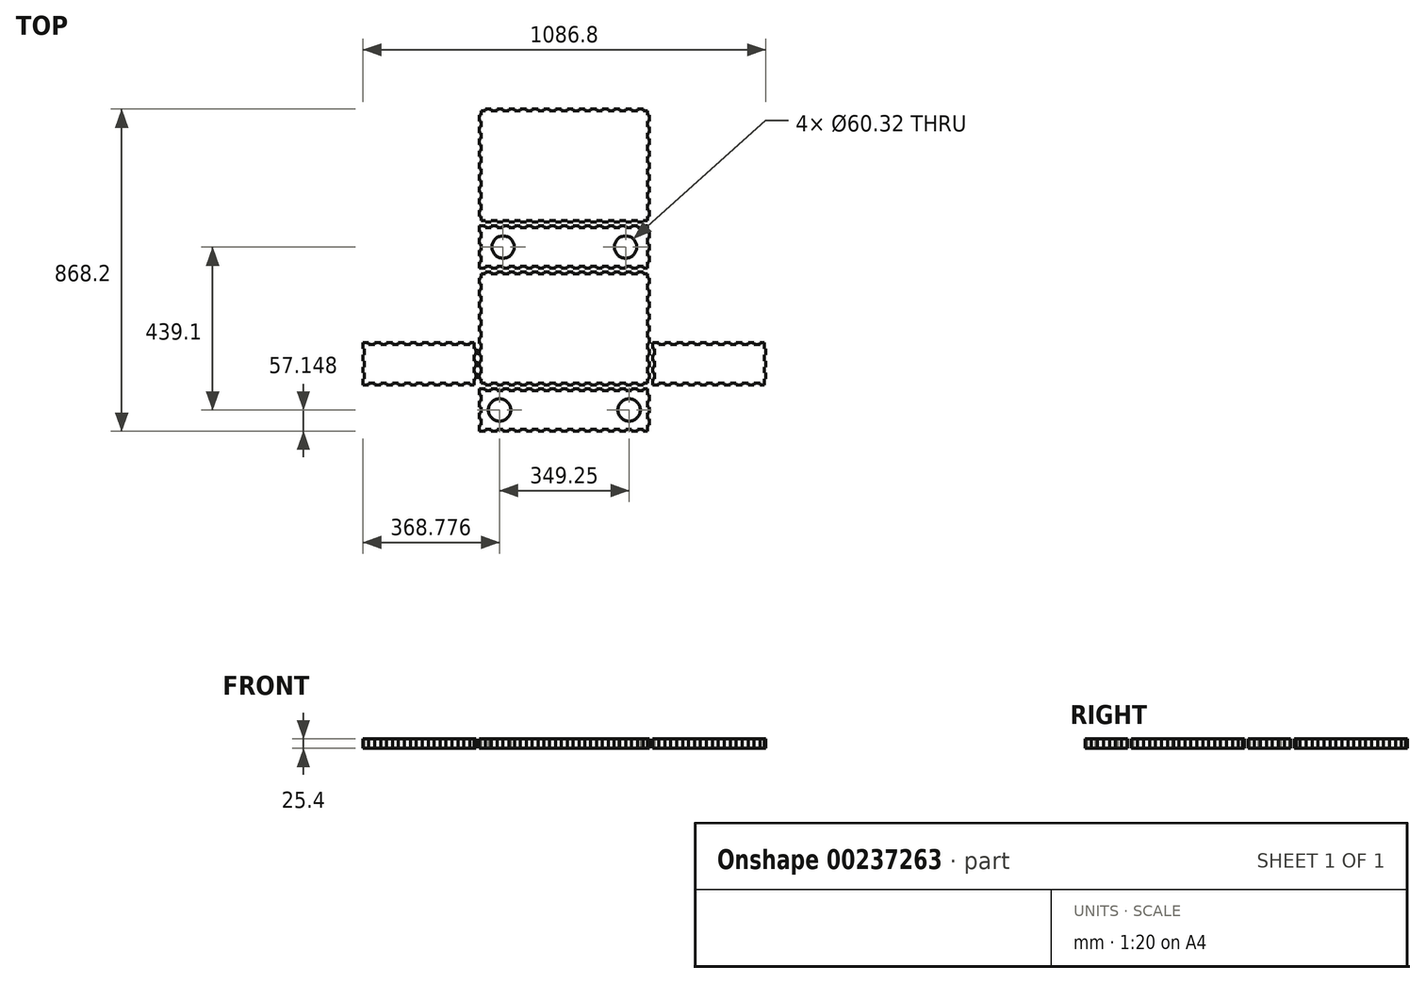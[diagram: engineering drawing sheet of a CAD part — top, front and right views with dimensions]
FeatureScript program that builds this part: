
annotation { "Feature Type Name" : "Feature", "Feature Type Description" : "" }
export const myFeature = defineFeature(function(context is Context, id is Id, definition is map)
    precondition{}
    {
        {
            var Q0;
            Q0=qCreatedBy(makeId("Top.planeOp"),FACE);
            var sketch = newSketch(context, id + "F0", { "sketchPlane" : qUnion([Q0])});
            skLineSegment(sketch, "E0", {"start": v(-228.6, -434.1) * mm, "end": v(-212.83, -434.1) * mm});
            skLineSegment(sketch, "E1", {"start": v(-212.83, -429.34) * mm, "end": v(-212.83, -434.1) * mm});
            skLineSegment(sketch, "E2", {"start": v(-212.83, -429.34) * mm, "end": v(-197.07, -429.34) * mm});
            skLineSegment(sketch, "E3", {"start": v(-197.07, -429.34) * mm, "end": v(-197.07, -434.1) * mm});
            skLineSegment(sketch, "E4", {"start": v(-197.07, -434.1) * mm, "end": v(-181.3, -434.1) * mm});
            skLineSegment(sketch, "E5", {"start": v(-181.3, -429.34) * mm, "end": v(-181.3, -434.1) * mm});
            skLineSegment(sketch, "E6", {"start": v(-181.3, -429.34) * mm, "end": v(-165.54, -429.34) * mm});
            skLineSegment(sketch, "E7", {"start": v(-165.54, -429.34) * mm, "end": v(-165.54, -434.1) * mm});
            skLineSegment(sketch, "E8", {"start": v(-165.54, -434.1) * mm, "end": v(-149.77, -434.1) * mm});
            skLineSegment(sketch, "E9", {"start": v(-149.77, -429.34) * mm, "end": v(-149.77, -434.1) * mm});
            skLineSegment(sketch, "E10", {"start": v(-149.77, -429.34) * mm, "end": v(-134, -429.34) * mm});
            skLineSegment(sketch, "E11", {"start": v(-134, -429.34) * mm, "end": v(-134, -434.1) * mm});
            skLineSegment(sketch, "E12", {"start": v(-134, -434.1) * mm, "end": v(-118.24, -434.1) * mm});
            skLineSegment(sketch, "E13", {"start": v(-118.24, -429.34) * mm, "end": v(-118.24, -434.1) * mm});
            skLineSegment(sketch, "E14", {"start": v(-118.24, -429.34) * mm, "end": v(-102.48, -429.34) * mm});
            skLineSegment(sketch, "E15", {"start": v(-102.48, -429.34) * mm, "end": v(-102.48, -434.1) * mm});
            skLineSegment(sketch, "E16", {"start": v(-102.48, -434.1) * mm, "end": v(-86.71, -434.1) * mm});
            skLineSegment(sketch, "E17", {"start": v(-86.71, -429.34) * mm, "end": v(-86.71, -434.1) * mm});
            skLineSegment(sketch, "E18", {"start": v(-86.71, -429.34) * mm, "end": v(-70.94, -429.34) * mm});
            skLineSegment(sketch, "E19", {"start": v(-70.94, -429.34) * mm, "end": v(-70.94, -434.1) * mm});
            skLineSegment(sketch, "E20", {"start": v(-70.94, -434.1) * mm, "end": v(-55.18, -434.1) * mm});
            skLineSegment(sketch, "E21", {"start": v(-55.18, -429.34) * mm, "end": v(-55.18, -434.1) * mm});
            skLineSegment(sketch, "E22", {"start": v(-55.18, -429.34) * mm, "end": v(-39.41, -429.34) * mm});
            skLineSegment(sketch, "E23", {"start": v(-39.41, -429.34) * mm, "end": v(-39.41, -434.1) * mm});
            skLineSegment(sketch, "E24", {"start": v(-39.41, -434.1) * mm, "end": v(-23.65, -434.1) * mm});
            skLineSegment(sketch, "E25", {"start": v(-23.65, -429.34) * mm, "end": v(-23.65, -434.1) * mm});
            skLineSegment(sketch, "E26", {"start": v(-23.65, -429.34) * mm, "end": v(-7.88, -429.34) * mm});
            skLineSegment(sketch, "E27", {"start": v(-7.88, -429.34) * mm, "end": v(-7.88, -434.1) * mm});
            skLineSegment(sketch, "E28", {"start": v(-7.88, -434.1) * mm, "end": v(7.88, -434.1) * mm});
            skLineSegment(sketch, "E29", {"start": v(7.88, -429.34) * mm, "end": v(7.88, -434.1) * mm});
            skLineSegment(sketch, "E30", {"start": v(7.88, -429.34) * mm, "end": v(23.65, -429.34) * mm});
            skLineSegment(sketch, "E31", {"start": v(23.65, -429.34) * mm, "end": v(23.65, -434.1) * mm});
            skLineSegment(sketch, "E32", {"start": v(23.65, -434.1) * mm, "end": v(39.42, -434.1) * mm});
            skLineSegment(sketch, "E33", {"start": v(39.42, -429.34) * mm, "end": v(39.42, -434.1) * mm});
            skLineSegment(sketch, "E34", {"start": v(39.42, -429.34) * mm, "end": v(55.18, -429.34) * mm});
            skLineSegment(sketch, "E35", {"start": v(55.18, -429.34) * mm, "end": v(55.18, -434.1) * mm});
            skLineSegment(sketch, "E36", {"start": v(55.18, -434.1) * mm, "end": v(70.95, -434.1) * mm});
            skLineSegment(sketch, "E37", {"start": v(70.95, -429.34) * mm, "end": v(70.95, -434.1) * mm});
            skLineSegment(sketch, "E38", {"start": v(70.95, -429.34) * mm, "end": v(86.7, -429.34) * mm});
            skLineSegment(sketch, "E39", {"start": v(86.7, -429.34) * mm, "end": v(86.7, -434.1) * mm});
            skLineSegment(sketch, "E40", {"start": v(86.7, -434.1) * mm, "end": v(102.48, -434.1) * mm});
            skLineSegment(sketch, "E41", {"start": v(102.48, -429.34) * mm, "end": v(102.48, -434.1) * mm});
            skLineSegment(sketch, "E42", {"start": v(102.48, -429.34) * mm, "end": v(118.24, -429.34) * mm});
            skLineSegment(sketch, "E43", {"start": v(118.24, -429.34) * mm, "end": v(118.24, -434.1) * mm});
            skLineSegment(sketch, "E44", {"start": v(118.24, -434.1) * mm, "end": v(134, -434.1) * mm});
            skLineSegment(sketch, "E45", {"start": v(134, -429.34) * mm, "end": v(134, -434.1) * mm});
            skLineSegment(sketch, "E46", {"start": v(134, -429.34) * mm, "end": v(149.77, -429.34) * mm});
            skLineSegment(sketch, "E47", {"start": v(149.77, -429.34) * mm, "end": v(149.77, -434.1) * mm});
            skLineSegment(sketch, "E48", {"start": v(149.77, -434.1) * mm, "end": v(165.54, -434.1) * mm});
            skLineSegment(sketch, "E49", {"start": v(165.54, -429.34) * mm, "end": v(165.54, -434.1) * mm});
            skLineSegment(sketch, "E50", {"start": v(165.54, -429.34) * mm, "end": v(181.3, -429.34) * mm});
            skLineSegment(sketch, "E51", {"start": v(181.3, -429.34) * mm, "end": v(181.3, -434.1) * mm});
            skLineSegment(sketch, "E52", {"start": v(181.3, -434.1) * mm, "end": v(197.07, -434.1) * mm});
            skLineSegment(sketch, "E53", {"start": v(197.07, -429.34) * mm, "end": v(197.07, -434.1) * mm});
            skLineSegment(sketch, "E54", {"start": v(197.07, -429.34) * mm, "end": v(212.83, -429.34) * mm});
            skLineSegment(sketch, "E55", {"start": v(212.83, -429.34) * mm, "end": v(212.83, -434.1) * mm});
            skLineSegment(sketch, "E56", {"start": v(212.83, -434.1) * mm, "end": v(223.84, -434.1) * mm});
            skLineSegment(sketch, "E57", {"start": v(-228.6, -319.8) * mm, "end": v(-212.83, -319.8) * mm});
            skLineSegment(sketch, "E58", {"start": v(-212.83, -319.8) * mm, "end": v(-212.83, -324.56) * mm});
            skLineSegment(sketch, "E59", {"start": v(-212.83, -324.56) * mm, "end": v(-197.07, -324.56) * mm});
            skLineSegment(sketch, "E60", {"start": v(-197.07, -319.8) * mm, "end": v(-197.07, -324.56) * mm});
            skLineSegment(sketch, "E61", {"start": v(-197.07, -319.8) * mm, "end": v(-181.3, -319.8) * mm});
            skLineSegment(sketch, "E62", {"start": v(-181.3, -319.8) * mm, "end": v(-181.3, -324.56) * mm});
            skLineSegment(sketch, "E63", {"start": v(-181.3, -324.56) * mm, "end": v(-165.54, -324.56) * mm});
            skLineSegment(sketch, "E64", {"start": v(-165.54, -319.8) * mm, "end": v(-165.54, -324.56) * mm});
            skLineSegment(sketch, "E65", {"start": v(-165.54, -319.8) * mm, "end": v(-149.77, -319.8) * mm});
            skLineSegment(sketch, "E66", {"start": v(-149.77, -319.8) * mm, "end": v(-149.77, -324.56) * mm});
            skLineSegment(sketch, "E67", {"start": v(-149.77, -324.56) * mm, "end": v(-134, -324.56) * mm});
            skLineSegment(sketch, "E68", {"start": v(-134, -319.8) * mm, "end": v(-134, -324.56) * mm});
            skLineSegment(sketch, "E69", {"start": v(-134, -319.8) * mm, "end": v(-118.24, -319.8) * mm});
            skLineSegment(sketch, "E70", {"start": v(-118.24, -319.8) * mm, "end": v(-118.24, -324.56) * mm});
            skLineSegment(sketch, "E71", {"start": v(-118.24, -324.56) * mm, "end": v(-102.48, -324.56) * mm});
            skLineSegment(sketch, "E72", {"start": v(-102.48, -319.8) * mm, "end": v(-102.48, -324.56) * mm});
            skLineSegment(sketch, "E73", {"start": v(-102.48, -319.8) * mm, "end": v(-86.71, -319.8) * mm});
            skLineSegment(sketch, "E74", {"start": v(-86.71, -319.8) * mm, "end": v(-86.71, -324.56) * mm});
            skLineSegment(sketch, "E75", {"start": v(-86.71, -324.56) * mm, "end": v(-70.94, -324.56) * mm});
            skLineSegment(sketch, "E76", {"start": v(-70.94, -319.8) * mm, "end": v(-70.94, -324.56) * mm});
            skLineSegment(sketch, "E77", {"start": v(-70.94, -319.8) * mm, "end": v(-55.18, -319.8) * mm});
            skLineSegment(sketch, "E78", {"start": v(-55.18, -319.8) * mm, "end": v(-55.18, -324.56) * mm});
            skLineSegment(sketch, "E79", {"start": v(-55.18, -324.56) * mm, "end": v(-39.41, -324.56) * mm});
            skLineSegment(sketch, "E80", {"start": v(-39.41, -319.8) * mm, "end": v(-39.41, -324.56) * mm});
            skLineSegment(sketch, "E81", {"start": v(-39.41, -319.8) * mm, "end": v(-23.65, -319.8) * mm});
            skLineSegment(sketch, "E82", {"start": v(-23.65, -319.8) * mm, "end": v(-23.65, -324.56) * mm});
            skLineSegment(sketch, "E83", {"start": v(-23.65, -324.56) * mm, "end": v(-7.88, -324.56) * mm});
            skLineSegment(sketch, "E84", {"start": v(-7.88, -319.8) * mm, "end": v(-7.88, -324.56) * mm});
            skLineSegment(sketch, "E85", {"start": v(-7.88, -319.8) * mm, "end": v(7.88, -319.8) * mm});
            skLineSegment(sketch, "E86", {"start": v(7.88, -319.8) * mm, "end": v(7.88, -324.56) * mm});
            skLineSegment(sketch, "E87", {"start": v(7.88, -324.56) * mm, "end": v(23.65, -324.56) * mm});
            skLineSegment(sketch, "E88", {"start": v(23.65, -319.8) * mm, "end": v(23.65, -324.56) * mm});
            skLineSegment(sketch, "E89", {"start": v(23.65, -319.8) * mm, "end": v(39.42, -319.8) * mm});
            skLineSegment(sketch, "E90", {"start": v(39.42, -319.8) * mm, "end": v(39.42, -324.56) * mm});
            skLineSegment(sketch, "E91", {"start": v(39.42, -324.56) * mm, "end": v(55.18, -324.56) * mm});
            skLineSegment(sketch, "E92", {"start": v(55.18, -319.8) * mm, "end": v(55.18, -324.56) * mm});
            skLineSegment(sketch, "E93", {"start": v(55.18, -319.8) * mm, "end": v(70.95, -319.8) * mm});
            skLineSegment(sketch, "E94", {"start": v(70.95, -319.8) * mm, "end": v(70.95, -324.56) * mm});
            skLineSegment(sketch, "E95", {"start": v(70.95, -324.56) * mm, "end": v(86.7, -324.56) * mm});
            skLineSegment(sketch, "E96", {"start": v(86.7, -319.8) * mm, "end": v(86.7, -324.56) * mm});
            skLineSegment(sketch, "E97", {"start": v(86.7, -319.8) * mm, "end": v(102.48, -319.8) * mm});
            skLineSegment(sketch, "E98", {"start": v(102.48, -319.8) * mm, "end": v(102.48, -324.56) * mm});
            skLineSegment(sketch, "E99", {"start": v(102.48, -324.56) * mm, "end": v(118.24, -324.56) * mm});
            skLineSegment(sketch, "E100", {"start": v(118.24, -319.8) * mm, "end": v(118.24, -324.56) * mm});
            skLineSegment(sketch, "E101", {"start": v(118.24, -319.8) * mm, "end": v(134, -319.8) * mm});
            skLineSegment(sketch, "E102", {"start": v(134, -319.8) * mm, "end": v(134, -324.56) * mm});
            skLineSegment(sketch, "E103", {"start": v(134, -324.56) * mm, "end": v(149.77, -324.56) * mm});
            skLineSegment(sketch, "E104", {"start": v(149.77, -319.8) * mm, "end": v(149.77, -324.56) * mm});
            skLineSegment(sketch, "E105", {"start": v(149.77, -319.8) * mm, "end": v(165.54, -319.8) * mm});
            skLineSegment(sketch, "E106", {"start": v(165.54, -319.8) * mm, "end": v(165.54, -324.56) * mm});
            skLineSegment(sketch, "E107", {"start": v(165.54, -324.56) * mm, "end": v(181.3, -324.56) * mm});
            skLineSegment(sketch, "E108", {"start": v(181.3, -319.8) * mm, "end": v(181.3, -324.56) * mm});
            skLineSegment(sketch, "E109", {"start": v(181.3, -319.8) * mm, "end": v(197.07, -319.8) * mm});
            skLineSegment(sketch, "E110", {"start": v(197.07, -319.8) * mm, "end": v(197.07, -324.56) * mm});
            skLineSegment(sketch, "E111", {"start": v(197.07, -324.56) * mm, "end": v(212.83, -324.56) * mm});
            skLineSegment(sketch, "E112", {"start": v(212.83, -319.8) * mm, "end": v(212.83, -324.56) * mm});
            skLineSegment(sketch, "E113", {"start": v(212.83, -319.8) * mm, "end": v(223.84, -319.8) * mm});
            skLineSegment(sketch, "E114", {"start": v(-228.6, -434.1) * mm, "end": v(-228.6, -417.77) * mm});
            skLineSegment(sketch, "E115", {"start": v(-223.84, -417.77) * mm, "end": v(-228.6, -417.77) * mm});
            skLineSegment(sketch, "E116", {"start": v(-223.84, -417.77) * mm, "end": v(-223.84, -401.44) * mm});
            skLineSegment(sketch, "E117", {"start": v(-223.84, -401.44) * mm, "end": v(-228.6, -401.44) * mm});
            skLineSegment(sketch, "E118", {"start": v(-228.6, -401.44) * mm, "end": v(-228.6, -385.12) * mm});
            skLineSegment(sketch, "E119", {"start": v(-223.84, -385.12) * mm, "end": v(-228.6, -385.12) * mm});
            skLineSegment(sketch, "E120", {"start": v(-223.84, -385.12) * mm, "end": v(-223.84, -368.79) * mm});
            skLineSegment(sketch, "E121", {"start": v(-223.84, -368.79) * mm, "end": v(-228.6, -368.79) * mm});
            skLineSegment(sketch, "E122", {"start": v(-228.6, -368.79) * mm, "end": v(-228.6, -352.46) * mm});
            skLineSegment(sketch, "E123", {"start": v(-223.84, -352.46) * mm, "end": v(-228.6, -352.46) * mm});
            skLineSegment(sketch, "E124", {"start": v(-223.84, -352.46) * mm, "end": v(-223.84, -336.13) * mm});
            skLineSegment(sketch, "E125", {"start": v(-223.84, -336.13) * mm, "end": v(-228.6, -336.13) * mm});
            skLineSegment(sketch, "E126", {"start": v(-228.6, -336.13) * mm, "end": v(-228.6, -319.8) * mm});
            skLineSegment(sketch, "E127", {"start": v(223.84, -434.1) * mm, "end": v(223.84, -417.77) * mm});
            skLineSegment(sketch, "E128", {"start": v(228.6, -417.77) * mm, "end": v(223.84, -417.77) * mm});
            skLineSegment(sketch, "E129", {"start": v(228.6, -417.77) * mm, "end": v(228.6, -401.44) * mm});
            skLineSegment(sketch, "E130", {"start": v(228.6, -401.44) * mm, "end": v(223.84, -401.44) * mm});
            skLineSegment(sketch, "E131", {"start": v(223.84, -401.44) * mm, "end": v(223.84, -385.12) * mm});
            skLineSegment(sketch, "E132", {"start": v(228.6, -385.12) * mm, "end": v(223.84, -385.12) * mm});
            skLineSegment(sketch, "E133", {"start": v(228.6, -385.12) * mm, "end": v(228.6, -368.79) * mm});
            skLineSegment(sketch, "E134", {"start": v(228.6, -368.79) * mm, "end": v(223.84, -368.79) * mm});
            skLineSegment(sketch, "E135", {"start": v(223.84, -368.79) * mm, "end": v(223.84, -352.46) * mm});
            skLineSegment(sketch, "E136", {"start": v(228.6, -352.46) * mm, "end": v(223.84, -352.46) * mm});
            skLineSegment(sketch, "E137", {"start": v(228.6, -352.46) * mm, "end": v(228.6, -336.13) * mm});
            skLineSegment(sketch, "E138", {"start": v(228.6, -336.13) * mm, "end": v(223.84, -336.13) * mm});
            skLineSegment(sketch, "E139", {"start": v(223.84, -336.13) * mm, "end": v(223.84, -319.8) * mm});
            skLineSegment(sketch, "E140", {"start": v(-543.4, -309.8) * mm, "end": v(-527.36, -309.8) * mm});
            skLineSegment(sketch, "E141", {"start": v(-527.36, -305.04) * mm, "end": v(-527.36, -309.8) * mm});
            skLineSegment(sketch, "E142", {"start": v(-527.36, -305.04) * mm, "end": v(-511.32, -305.04) * mm});
            skLineSegment(sketch, "E143", {"start": v(-511.32, -305.04) * mm, "end": v(-511.32, -309.8) * mm});
            skLineSegment(sketch, "E144", {"start": v(-511.32, -309.8) * mm, "end": v(-495.27, -309.8) * mm});
            skLineSegment(sketch, "E145", {"start": v(-495.27, -305.04) * mm, "end": v(-495.27, -309.8) * mm});
            skLineSegment(sketch, "E146", {"start": v(-495.27, -305.04) * mm, "end": v(-479.23, -305.04) * mm});
            skLineSegment(sketch, "E147", {"start": v(-479.23, -305.04) * mm, "end": v(-479.23, -309.8) * mm});
            skLineSegment(sketch, "E148", {"start": v(-479.23, -309.8) * mm, "end": v(-463.19, -309.8) * mm});
            skLineSegment(sketch, "E149", {"start": v(-463.19, -305.04) * mm, "end": v(-463.19, -309.8) * mm});
            skLineSegment(sketch, "E150", {"start": v(-463.19, -305.04) * mm, "end": v(-447.15, -305.04) * mm});
            skLineSegment(sketch, "E151", {"start": v(-447.15, -305.04) * mm, "end": v(-447.15, -309.8) * mm});
            skLineSegment(sketch, "E152", {"start": v(-447.15, -309.8) * mm, "end": v(-431.1, -309.8) * mm});
            skLineSegment(sketch, "E153", {"start": v(-431.1, -305.04) * mm, "end": v(-431.1, -309.8) * mm});
            skLineSegment(sketch, "E154", {"start": v(-431.1, -305.04) * mm, "end": v(-415.06, -305.04) * mm});
            skLineSegment(sketch, "E155", {"start": v(-415.06, -305.04) * mm, "end": v(-415.06, -309.8) * mm});
            skLineSegment(sketch, "E156", {"start": v(-415.06, -309.8) * mm, "end": v(-399.02, -309.8) * mm});
            skLineSegment(sketch, "E157", {"start": v(-399.02, -305.04) * mm, "end": v(-399.02, -309.8) * mm});
            skLineSegment(sketch, "E158", {"start": v(-399.02, -305.04) * mm, "end": v(-382.98, -305.04) * mm});
            skLineSegment(sketch, "E159", {"start": v(-382.98, -305.04) * mm, "end": v(-382.98, -309.8) * mm});
            skLineSegment(sketch, "E160", {"start": v(-382.98, -309.8) * mm, "end": v(-366.94, -309.8) * mm});
            skLineSegment(sketch, "E161", {"start": v(-366.94, -305.04) * mm, "end": v(-366.94, -309.8) * mm});
            skLineSegment(sketch, "E162", {"start": v(-366.94, -305.04) * mm, "end": v(-350.9, -305.04) * mm});
            skLineSegment(sketch, "E163", {"start": v(-350.9, -305.04) * mm, "end": v(-350.9, -309.8) * mm});
            skLineSegment(sketch, "E164", {"start": v(-350.9, -309.8) * mm, "end": v(-334.85, -309.8) * mm});
            skLineSegment(sketch, "E165", {"start": v(-334.85, -305.04) * mm, "end": v(-334.85, -309.8) * mm});
            skLineSegment(sketch, "E166", {"start": v(-334.85, -305.04) * mm, "end": v(-318.81, -305.04) * mm});
            skLineSegment(sketch, "E167", {"start": v(-318.81, -305.04) * mm, "end": v(-318.81, -309.8) * mm});
            skLineSegment(sketch, "E168", {"start": v(-318.81, -309.8) * mm, "end": v(-302.77, -309.8) * mm});
            skLineSegment(sketch, "E169", {"start": v(-302.77, -305.04) * mm, "end": v(-302.77, -309.8) * mm});
            skLineSegment(sketch, "E170", {"start": v(-302.77, -305.04) * mm, "end": v(-286.73, -305.04) * mm});
            skLineSegment(sketch, "E171", {"start": v(-286.73, -305.04) * mm, "end": v(-286.73, -309.8) * mm});
            skLineSegment(sketch, "E172", {"start": v(-286.73, -309.8) * mm, "end": v(-270.69, -309.8) * mm});
            skLineSegment(sketch, "E173", {"start": v(-270.69, -305.04) * mm, "end": v(-270.69, -309.8) * mm});
            skLineSegment(sketch, "E174", {"start": v(-270.69, -305.04) * mm, "end": v(-254.64, -305.04) * mm});
            skLineSegment(sketch, "E175", {"start": v(-254.64, -305.04) * mm, "end": v(-254.64, -309.8) * mm});
            skLineSegment(sketch, "E176", {"start": v(-254.64, -309.8) * mm, "end": v(-243.36, -309.8) * mm});
            skLineSegment(sketch, "E177", {"start": v(-543.4, -195.5) * mm, "end": v(-527.36, -195.5) * mm});
            skLineSegment(sketch, "E178", {"start": v(-527.36, -195.5) * mm, "end": v(-527.36, -200.26) * mm});
            skLineSegment(sketch, "E179", {"start": v(-527.36, -200.26) * mm, "end": v(-511.32, -200.26) * mm});
            skLineSegment(sketch, "E180", {"start": v(-511.32, -195.5) * mm, "end": v(-511.32, -200.26) * mm});
            skLineSegment(sketch, "E181", {"start": v(-511.32, -195.5) * mm, "end": v(-495.27, -195.5) * mm});
            skLineSegment(sketch, "E182", {"start": v(-495.27, -195.5) * mm, "end": v(-495.27, -200.26) * mm});
            skLineSegment(sketch, "E183", {"start": v(-495.27, -200.26) * mm, "end": v(-479.23, -200.26) * mm});
            skLineSegment(sketch, "E184", {"start": v(-479.23, -195.5) * mm, "end": v(-479.23, -200.26) * mm});
            skLineSegment(sketch, "E185", {"start": v(-479.23, -195.5) * mm, "end": v(-463.19, -195.5) * mm});
            skLineSegment(sketch, "E186", {"start": v(-463.19, -195.5) * mm, "end": v(-463.19, -200.26) * mm});
            skLineSegment(sketch, "E187", {"start": v(-463.19, -200.26) * mm, "end": v(-447.15, -200.26) * mm});
            skLineSegment(sketch, "E188", {"start": v(-447.15, -195.5) * mm, "end": v(-447.15, -200.26) * mm});
            skLineSegment(sketch, "E189", {"start": v(-447.15, -195.5) * mm, "end": v(-431.1, -195.5) * mm});
            skLineSegment(sketch, "E190", {"start": v(-431.1, -195.5) * mm, "end": v(-431.1, -200.26) * mm});
            skLineSegment(sketch, "E191", {"start": v(-431.1, -200.26) * mm, "end": v(-415.06, -200.26) * mm});
            skLineSegment(sketch, "E192", {"start": v(-415.06, -195.5) * mm, "end": v(-415.06, -200.26) * mm});
            skLineSegment(sketch, "E193", {"start": v(-415.06, -195.5) * mm, "end": v(-399.02, -195.5) * mm});
            skLineSegment(sketch, "E194", {"start": v(-399.02, -195.5) * mm, "end": v(-399.02, -200.26) * mm});
            skLineSegment(sketch, "E195", {"start": v(-399.02, -200.26) * mm, "end": v(-382.98, -200.26) * mm});
            skLineSegment(sketch, "E196", {"start": v(-382.98, -195.5) * mm, "end": v(-382.98, -200.26) * mm});
            skLineSegment(sketch, "E197", {"start": v(-382.98, -195.5) * mm, "end": v(-366.94, -195.5) * mm});
            skLineSegment(sketch, "E198", {"start": v(-366.94, -195.5) * mm, "end": v(-366.94, -200.26) * mm});
            skLineSegment(sketch, "E199", {"start": v(-366.94, -200.26) * mm, "end": v(-350.9, -200.26) * mm});
            skLineSegment(sketch, "E200", {"start": v(-350.9, -195.5) * mm, "end": v(-350.9, -200.26) * mm});
            skLineSegment(sketch, "E201", {"start": v(-350.9, -195.5) * mm, "end": v(-334.85, -195.5) * mm});
            skLineSegment(sketch, "E202", {"start": v(-334.85, -195.5) * mm, "end": v(-334.85, -200.26) * mm});
            skLineSegment(sketch, "E203", {"start": v(-334.85, -200.26) * mm, "end": v(-318.81, -200.26) * mm});
            skLineSegment(sketch, "E204", {"start": v(-318.81, -195.5) * mm, "end": v(-318.81, -200.26) * mm});
            skLineSegment(sketch, "E205", {"start": v(-318.81, -195.5) * mm, "end": v(-302.77, -195.5) * mm});
            skLineSegment(sketch, "E206", {"start": v(-302.77, -195.5) * mm, "end": v(-302.77, -200.26) * mm});
            skLineSegment(sketch, "E207", {"start": v(-302.77, -200.26) * mm, "end": v(-286.73, -200.26) * mm});
            skLineSegment(sketch, "E208", {"start": v(-286.73, -195.5) * mm, "end": v(-286.73, -200.26) * mm});
            skLineSegment(sketch, "E209", {"start": v(-286.73, -195.5) * mm, "end": v(-270.69, -195.5) * mm});
            skLineSegment(sketch, "E210", {"start": v(-270.69, -195.5) * mm, "end": v(-270.69, -200.26) * mm});
            skLineSegment(sketch, "E211", {"start": v(-270.69, -200.26) * mm, "end": v(-254.64, -200.26) * mm});
            skLineSegment(sketch, "E212", {"start": v(-254.64, -195.5) * mm, "end": v(-254.64, -200.26) * mm});
            skLineSegment(sketch, "E213", {"start": v(-254.64, -195.5) * mm, "end": v(-243.36, -195.5) * mm});
            skLineSegment(sketch, "E214", {"start": v(-543.4, -309.8) * mm, "end": v(-543.4, -293.47) * mm});
            skLineSegment(sketch, "E215", {"start": v(-538.64, -293.47) * mm, "end": v(-543.4, -293.47) * mm});
            skLineSegment(sketch, "E216", {"start": v(-538.64, -293.47) * mm, "end": v(-538.64, -277.14) * mm});
            skLineSegment(sketch, "E217", {"start": v(-538.64, -277.14) * mm, "end": v(-543.4, -277.14) * mm});
            skLineSegment(sketch, "E218", {"start": v(-543.4, -277.14) * mm, "end": v(-543.4, -260.82) * mm});
            skLineSegment(sketch, "E219", {"start": v(-538.64, -260.82) * mm, "end": v(-543.4, -260.82) * mm});
            skLineSegment(sketch, "E220", {"start": v(-538.64, -260.82) * mm, "end": v(-538.64, -244.49) * mm});
            skLineSegment(sketch, "E221", {"start": v(-538.64, -244.49) * mm, "end": v(-543.4, -244.49) * mm});
            skLineSegment(sketch, "E222", {"start": v(-543.4, -244.49) * mm, "end": v(-543.4, -228.16) * mm});
            skLineSegment(sketch, "E223", {"start": v(-538.64, -228.16) * mm, "end": v(-543.4, -228.16) * mm});
            skLineSegment(sketch, "E224", {"start": v(-538.64, -228.16) * mm, "end": v(-538.64, -211.83) * mm});
            skLineSegment(sketch, "E225", {"start": v(-538.64, -211.83) * mm, "end": v(-543.4, -211.83) * mm});
            skLineSegment(sketch, "E226", {"start": v(-543.4, -211.83) * mm, "end": v(-543.4, -195.5) * mm});
            skLineSegment(sketch, "E227", {"start": v(-243.36, -309.8) * mm, "end": v(-243.36, -293.47) * mm});
            skLineSegment(sketch, "E228", {"start": v(-238.6, -293.47) * mm, "end": v(-243.36, -293.47) * mm});
            skLineSegment(sketch, "E229", {"start": v(-238.6, -293.47) * mm, "end": v(-238.6, -277.14) * mm});
            skLineSegment(sketch, "E230", {"start": v(-238.6, -277.14) * mm, "end": v(-243.36, -277.14) * mm});
            skLineSegment(sketch, "E231", {"start": v(-243.36, -277.14) * mm, "end": v(-243.36, -260.82) * mm});
            skLineSegment(sketch, "E232", {"start": v(-238.6, -260.82) * mm, "end": v(-243.36, -260.82) * mm});
            skLineSegment(sketch, "E233", {"start": v(-238.6, -260.82) * mm, "end": v(-238.6, -244.49) * mm});
            skLineSegment(sketch, "E234", {"start": v(-238.6, -244.49) * mm, "end": v(-243.36, -244.49) * mm});
            skLineSegment(sketch, "E235", {"start": v(-243.36, -244.49) * mm, "end": v(-243.36, -228.16) * mm});
            skLineSegment(sketch, "E236", {"start": v(-238.6, -228.16) * mm, "end": v(-243.36, -228.16) * mm});
            skLineSegment(sketch, "E237", {"start": v(-238.6, -228.16) * mm, "end": v(-238.6, -211.83) * mm});
            skLineSegment(sketch, "E238", {"start": v(-238.6, -211.83) * mm, "end": v(-243.36, -211.83) * mm});
            skLineSegment(sketch, "E239", {"start": v(-243.36, -211.83) * mm, "end": v(-243.36, -195.5) * mm});
            skLineSegment(sketch, "E240", {"start": v(-223.84, -305.04) * mm, "end": v(-212.83, -305.04) * mm});
            skLineSegment(sketch, "E241", {"start": v(-212.83, -305.04) * mm, "end": v(-212.83, -309.8) * mm});
            skLineSegment(sketch, "E242", {"start": v(-212.83, -309.8) * mm, "end": v(-197.07, -309.8) * mm});
            skLineSegment(sketch, "E243", {"start": v(-197.07, -305.04) * mm, "end": v(-197.07, -309.8) * mm});
            skLineSegment(sketch, "E244", {"start": v(-197.07, -305.04) * mm, "end": v(-181.3, -305.04) * mm});
            skLineSegment(sketch, "E245", {"start": v(-181.3, -305.04) * mm, "end": v(-181.3, -309.8) * mm});
            skLineSegment(sketch, "E246", {"start": v(-181.3, -309.8) * mm, "end": v(-165.54, -309.8) * mm});
            skLineSegment(sketch, "E247", {"start": v(-165.54, -305.04) * mm, "end": v(-165.54, -309.8) * mm});
            skLineSegment(sketch, "E248", {"start": v(-165.54, -305.04) * mm, "end": v(-149.77, -305.04) * mm});
            skLineSegment(sketch, "E249", {"start": v(-149.77, -305.04) * mm, "end": v(-149.77, -309.8) * mm});
            skLineSegment(sketch, "E250", {"start": v(-149.77, -309.8) * mm, "end": v(-134, -309.8) * mm});
            skLineSegment(sketch, "E251", {"start": v(-134, -305.04) * mm, "end": v(-134, -309.8) * mm});
            skLineSegment(sketch, "E252", {"start": v(-134, -305.04) * mm, "end": v(-118.24, -305.04) * mm});
            skLineSegment(sketch, "E253", {"start": v(-118.24, -305.04) * mm, "end": v(-118.24, -309.8) * mm});
            skLineSegment(sketch, "E254", {"start": v(-118.24, -309.8) * mm, "end": v(-102.48, -309.8) * mm});
            skLineSegment(sketch, "E255", {"start": v(-102.48, -305.04) * mm, "end": v(-102.48, -309.8) * mm});
            skLineSegment(sketch, "E256", {"start": v(-102.48, -305.04) * mm, "end": v(-86.71, -305.04) * mm});
            skLineSegment(sketch, "E257", {"start": v(-86.71, -305.04) * mm, "end": v(-86.71, -309.8) * mm});
            skLineSegment(sketch, "E258", {"start": v(-86.71, -309.8) * mm, "end": v(-70.94, -309.8) * mm});
            skLineSegment(sketch, "E259", {"start": v(-70.94, -305.04) * mm, "end": v(-70.94, -309.8) * mm});
            skLineSegment(sketch, "E260", {"start": v(-70.94, -305.04) * mm, "end": v(-55.18, -305.04) * mm});
            skLineSegment(sketch, "E261", {"start": v(-55.18, -305.04) * mm, "end": v(-55.18, -309.8) * mm});
            skLineSegment(sketch, "E262", {"start": v(-55.18, -309.8) * mm, "end": v(-39.41, -309.8) * mm});
            skLineSegment(sketch, "E263", {"start": v(-39.41, -305.04) * mm, "end": v(-39.41, -309.8) * mm});
            skLineSegment(sketch, "E264", {"start": v(-39.41, -305.04) * mm, "end": v(-23.65, -305.04) * mm});
            skLineSegment(sketch, "E265", {"start": v(-23.65, -305.04) * mm, "end": v(-23.65, -309.8) * mm});
            skLineSegment(sketch, "E266", {"start": v(-23.65, -309.8) * mm, "end": v(-7.88, -309.8) * mm});
            skLineSegment(sketch, "E267", {"start": v(-7.88, -305.04) * mm, "end": v(-7.88, -309.8) * mm});
            skLineSegment(sketch, "E268", {"start": v(-7.88, -305.04) * mm, "end": v(7.88, -305.04) * mm});
            skLineSegment(sketch, "E269", {"start": v(7.88, -305.04) * mm, "end": v(7.88, -309.8) * mm});
            skLineSegment(sketch, "E270", {"start": v(7.88, -309.8) * mm, "end": v(23.65, -309.8) * mm});
            skLineSegment(sketch, "E271", {"start": v(23.65, -305.04) * mm, "end": v(23.65, -309.8) * mm});
            skLineSegment(sketch, "E272", {"start": v(23.65, -305.04) * mm, "end": v(39.42, -305.04) * mm});
            skLineSegment(sketch, "E273", {"start": v(39.42, -305.04) * mm, "end": v(39.42, -309.8) * mm});
            skLineSegment(sketch, "E274", {"start": v(39.42, -309.8) * mm, "end": v(55.18, -309.8) * mm});
            skLineSegment(sketch, "E275", {"start": v(55.18, -305.04) * mm, "end": v(55.18, -309.8) * mm});
            skLineSegment(sketch, "E276", {"start": v(55.18, -305.04) * mm, "end": v(70.95, -305.04) * mm});
            skLineSegment(sketch, "E277", {"start": v(70.95, -305.04) * mm, "end": v(70.95, -309.8) * mm});
            skLineSegment(sketch, "E278", {"start": v(70.95, -309.8) * mm, "end": v(86.7, -309.8) * mm});
            skLineSegment(sketch, "E279", {"start": v(86.7, -305.04) * mm, "end": v(86.7, -309.8) * mm});
            skLineSegment(sketch, "E280", {"start": v(86.7, -305.04) * mm, "end": v(102.48, -305.04) * mm});
            skLineSegment(sketch, "E281", {"start": v(102.48, -305.04) * mm, "end": v(102.48, -309.8) * mm});
            skLineSegment(sketch, "E282", {"start": v(102.48, -309.8) * mm, "end": v(118.24, -309.8) * mm});
            skLineSegment(sketch, "E283", {"start": v(118.24, -305.04) * mm, "end": v(118.24, -309.8) * mm});
            skLineSegment(sketch, "E284", {"start": v(118.24, -305.04) * mm, "end": v(134, -305.04) * mm});
            skLineSegment(sketch, "E285", {"start": v(134, -305.04) * mm, "end": v(134, -309.8) * mm});
            skLineSegment(sketch, "E286", {"start": v(134, -309.8) * mm, "end": v(149.77, -309.8) * mm});
            skLineSegment(sketch, "E287", {"start": v(149.77, -305.04) * mm, "end": v(149.77, -309.8) * mm});
            skLineSegment(sketch, "E288", {"start": v(149.77, -305.04) * mm, "end": v(165.54, -305.04) * mm});
            skLineSegment(sketch, "E289", {"start": v(165.54, -305.04) * mm, "end": v(165.54, -309.8) * mm});
            skLineSegment(sketch, "E290", {"start": v(165.54, -309.8) * mm, "end": v(181.3, -309.8) * mm});
            skLineSegment(sketch, "E291", {"start": v(181.3, -305.04) * mm, "end": v(181.3, -309.8) * mm});
            skLineSegment(sketch, "E292", {"start": v(181.3, -305.04) * mm, "end": v(197.07, -305.04) * mm});
            skLineSegment(sketch, "E293", {"start": v(197.07, -305.04) * mm, "end": v(197.07, -309.8) * mm});
            skLineSegment(sketch, "E294", {"start": v(197.07, -309.8) * mm, "end": v(212.83, -309.8) * mm});
            skLineSegment(sketch, "E295", {"start": v(212.83, -305.04) * mm, "end": v(212.83, -309.8) * mm});
            skLineSegment(sketch, "E296", {"start": v(212.83, -305.04) * mm, "end": v(223.84, -305.04) * mm});
            skLineSegment(sketch, "E297", {"start": v(-223.84, -9.76) * mm, "end": v(-212.83, -9.76) * mm});
            skLineSegment(sketch, "E298", {"start": v(-212.83, -5) * mm, "end": v(-212.83, -9.76) * mm});
            skLineSegment(sketch, "E299", {"start": v(-212.83, -5) * mm, "end": v(-197.07, -5) * mm});
            skLineSegment(sketch, "E300", {"start": v(-197.07, -5) * mm, "end": v(-197.07, -9.76) * mm});
            skLineSegment(sketch, "E301", {"start": v(-197.07, -9.76) * mm, "end": v(-181.3, -9.76) * mm});
            skLineSegment(sketch, "E302", {"start": v(-181.3, -5) * mm, "end": v(-181.3, -9.76) * mm});
            skLineSegment(sketch, "E303", {"start": v(-181.3, -5) * mm, "end": v(-165.54, -5) * mm});
            skLineSegment(sketch, "E304", {"start": v(-165.54, -5) * mm, "end": v(-165.54, -9.76) * mm});
            skLineSegment(sketch, "E305", {"start": v(-165.54, -9.76) * mm, "end": v(-149.77, -9.76) * mm});
            skLineSegment(sketch, "E306", {"start": v(-149.77, -5) * mm, "end": v(-149.77, -9.76) * mm});
            skLineSegment(sketch, "E307", {"start": v(-149.77, -5) * mm, "end": v(-134, -5) * mm});
            skLineSegment(sketch, "E308", {"start": v(-134, -5) * mm, "end": v(-134, -9.76) * mm});
            skLineSegment(sketch, "E309", {"start": v(-134, -9.76) * mm, "end": v(-118.24, -9.76) * mm});
            skLineSegment(sketch, "E310", {"start": v(-118.24, -5) * mm, "end": v(-118.24, -9.76) * mm});
            skLineSegment(sketch, "E311", {"start": v(-118.24, -5) * mm, "end": v(-102.48, -5) * mm});
            skLineSegment(sketch, "E312", {"start": v(-102.48, -5) * mm, "end": v(-102.48, -9.76) * mm});
            skLineSegment(sketch, "E313", {"start": v(-102.48, -9.76) * mm, "end": v(-86.71, -9.76) * mm});
            skLineSegment(sketch, "E314", {"start": v(-86.71, -5) * mm, "end": v(-86.71, -9.76) * mm});
            skLineSegment(sketch, "E315", {"start": v(-86.71, -5) * mm, "end": v(-70.94, -5) * mm});
            skLineSegment(sketch, "E316", {"start": v(-70.94, -5) * mm, "end": v(-70.94, -9.76) * mm});
            skLineSegment(sketch, "E317", {"start": v(-70.94, -9.76) * mm, "end": v(-55.18, -9.76) * mm});
            skLineSegment(sketch, "E318", {"start": v(-55.18, -5) * mm, "end": v(-55.18, -9.76) * mm});
            skLineSegment(sketch, "E319", {"start": v(-55.18, -5) * mm, "end": v(-39.41, -5) * mm});
            skLineSegment(sketch, "E320", {"start": v(-39.41, -5) * mm, "end": v(-39.41, -9.76) * mm});
            skLineSegment(sketch, "E321", {"start": v(-39.41, -9.76) * mm, "end": v(-23.65, -9.76) * mm});
            skLineSegment(sketch, "E322", {"start": v(-23.65, -5) * mm, "end": v(-23.65, -9.76) * mm});
            skLineSegment(sketch, "E323", {"start": v(-23.65, -5) * mm, "end": v(-7.88, -5) * mm});
            skLineSegment(sketch, "E324", {"start": v(-7.88, -5) * mm, "end": v(-7.88, -9.76) * mm});
            skLineSegment(sketch, "E325", {"start": v(-7.88, -9.76) * mm, "end": v(7.88, -9.76) * mm});
            skLineSegment(sketch, "E326", {"start": v(7.88, -5) * mm, "end": v(7.88, -9.76) * mm});
            skLineSegment(sketch, "E327", {"start": v(7.88, -5) * mm, "end": v(23.65, -5) * mm});
            skLineSegment(sketch, "E328", {"start": v(23.65, -5) * mm, "end": v(23.65, -9.76) * mm});
            skLineSegment(sketch, "E329", {"start": v(23.65, -9.76) * mm, "end": v(39.42, -9.76) * mm});
            skLineSegment(sketch, "E330", {"start": v(39.42, -5) * mm, "end": v(39.42, -9.76) * mm});
            skLineSegment(sketch, "E331", {"start": v(39.42, -5) * mm, "end": v(55.18, -5) * mm});
            skLineSegment(sketch, "E332", {"start": v(55.18, -5) * mm, "end": v(55.18, -9.76) * mm});
            skLineSegment(sketch, "E333", {"start": v(55.18, -9.76) * mm, "end": v(70.95, -9.76) * mm});
            skLineSegment(sketch, "E334", {"start": v(70.95, -5) * mm, "end": v(70.95, -9.76) * mm});
            skLineSegment(sketch, "E335", {"start": v(70.95, -5) * mm, "end": v(86.7, -5) * mm});
            skLineSegment(sketch, "E336", {"start": v(86.7, -5) * mm, "end": v(86.7, -9.76) * mm});
            skLineSegment(sketch, "E337", {"start": v(86.7, -9.76) * mm, "end": v(102.48, -9.76) * mm});
            skLineSegment(sketch, "E338", {"start": v(102.48, -5) * mm, "end": v(102.48, -9.76) * mm});
            skLineSegment(sketch, "E339", {"start": v(102.48, -5) * mm, "end": v(118.24, -5) * mm});
            skLineSegment(sketch, "E340", {"start": v(118.24, -5) * mm, "end": v(118.24, -9.76) * mm});
            skLineSegment(sketch, "E341", {"start": v(118.24, -9.76) * mm, "end": v(134, -9.76) * mm});
            skLineSegment(sketch, "E342", {"start": v(134, -5) * mm, "end": v(134, -9.76) * mm});
            skLineSegment(sketch, "E343", {"start": v(134, -5) * mm, "end": v(149.77, -5) * mm});
            skLineSegment(sketch, "E344", {"start": v(149.77, -5) * mm, "end": v(149.77, -9.76) * mm});
            skLineSegment(sketch, "E345", {"start": v(149.77, -9.76) * mm, "end": v(165.54, -9.76) * mm});
            skLineSegment(sketch, "E346", {"start": v(165.54, -5) * mm, "end": v(165.54, -9.76) * mm});
            skLineSegment(sketch, "E347", {"start": v(165.54, -5) * mm, "end": v(181.3, -5) * mm});
            skLineSegment(sketch, "E348", {"start": v(181.3, -5) * mm, "end": v(181.3, -9.76) * mm});
            skLineSegment(sketch, "E349", {"start": v(181.3, -9.76) * mm, "end": v(197.07, -9.76) * mm});
            skLineSegment(sketch, "E350", {"start": v(197.07, -5) * mm, "end": v(197.07, -9.76) * mm});
            skLineSegment(sketch, "E351", {"start": v(197.07, -5) * mm, "end": v(212.83, -5) * mm});
            skLineSegment(sketch, "E352", {"start": v(212.83, -5) * mm, "end": v(212.83, -9.76) * mm});
            skLineSegment(sketch, "E353", {"start": v(212.83, -9.76) * mm, "end": v(223.84, -9.76) * mm});
            skLineSegment(sketch, "E354", {"start": v(-223.84, -305.04) * mm, "end": v(-223.84, -293.76) * mm});
            skLineSegment(sketch, "E355", {"start": v(-223.84, -293.76) * mm, "end": v(-228.6, -293.76) * mm});
            skLineSegment(sketch, "E356", {"start": v(-228.6, -293.76) * mm, "end": v(-228.6, -277.72) * mm});
            skLineSegment(sketch, "E357", {"start": v(-223.84, -277.72) * mm, "end": v(-228.6, -277.72) * mm});
            skLineSegment(sketch, "E358", {"start": v(-223.84, -277.72) * mm, "end": v(-223.84, -261.68) * mm});
            skLineSegment(sketch, "E359", {"start": v(-223.84, -261.68) * mm, "end": v(-228.6, -261.68) * mm});
            skLineSegment(sketch, "E360", {"start": v(-228.6, -261.68) * mm, "end": v(-228.6, -245.63) * mm});
            skLineSegment(sketch, "E361", {"start": v(-223.84, -245.63) * mm, "end": v(-228.6, -245.63) * mm});
            skLineSegment(sketch, "E362", {"start": v(-223.84, -245.63) * mm, "end": v(-223.84, -229.6) * mm});
            skLineSegment(sketch, "E363", {"start": v(-223.84, -229.6) * mm, "end": v(-228.6, -229.6) * mm});
            skLineSegment(sketch, "E364", {"start": v(-228.6, -229.6) * mm, "end": v(-228.6, -213.55) * mm});
            skLineSegment(sketch, "E365", {"start": v(-223.84, -213.55) * mm, "end": v(-228.6, -213.55) * mm});
            skLineSegment(sketch, "E366", {"start": v(-223.84, -213.55) * mm, "end": v(-223.84, -197.5) * mm});
            skLineSegment(sketch, "E367", {"start": v(-223.84, -197.5) * mm, "end": v(-228.6, -197.5) * mm});
            skLineSegment(sketch, "E368", {"start": v(-228.6, -197.5) * mm, "end": v(-228.6, -181.47) * mm});
            skLineSegment(sketch, "E369", {"start": v(-223.84, -181.47) * mm, "end": v(-228.6, -181.47) * mm});
            skLineSegment(sketch, "E370", {"start": v(-223.84, -181.47) * mm, "end": v(-223.84, -165.42) * mm});
            skLineSegment(sketch, "E371", {"start": v(-223.84, -165.42) * mm, "end": v(-228.6, -165.42) * mm});
            skLineSegment(sketch, "E372", {"start": v(-228.6, -165.42) * mm, "end": v(-228.6, -149.38) * mm});
            skLineSegment(sketch, "E373", {"start": v(-223.84, -149.38) * mm, "end": v(-228.6, -149.38) * mm});
            skLineSegment(sketch, "E374", {"start": v(-223.84, -149.38) * mm, "end": v(-223.84, -133.34) * mm});
            skLineSegment(sketch, "E375", {"start": v(-223.84, -133.34) * mm, "end": v(-228.6, -133.34) * mm});
            skLineSegment(sketch, "E376", {"start": v(-228.6, -133.34) * mm, "end": v(-228.6, -117.3) * mm});
            skLineSegment(sketch, "E377", {"start": v(-223.84, -117.3) * mm, "end": v(-228.6, -117.3) * mm});
            skLineSegment(sketch, "E378", {"start": v(-223.84, -117.3) * mm, "end": v(-223.84, -101.25) * mm});
            skLineSegment(sketch, "E379", {"start": v(-223.84, -101.25) * mm, "end": v(-228.6, -101.25) * mm});
            skLineSegment(sketch, "E380", {"start": v(-228.6, -101.25) * mm, "end": v(-228.6, -85.21) * mm});
            skLineSegment(sketch, "E381", {"start": v(-223.84, -85.21) * mm, "end": v(-228.6, -85.21) * mm});
            skLineSegment(sketch, "E382", {"start": v(-223.84, -85.21) * mm, "end": v(-223.84, -69.17) * mm});
            skLineSegment(sketch, "E383", {"start": v(-223.84, -69.17) * mm, "end": v(-228.6, -69.17) * mm});
            skLineSegment(sketch, "E384", {"start": v(-228.6, -69.17) * mm, "end": v(-228.6, -53.13) * mm});
            skLineSegment(sketch, "E385", {"start": v(-223.84, -53.13) * mm, "end": v(-228.6, -53.13) * mm});
            skLineSegment(sketch, "E386", {"start": v(-223.84, -53.13) * mm, "end": v(-223.84, -37.08) * mm});
            skLineSegment(sketch, "E387", {"start": v(-223.84, -37.08) * mm, "end": v(-228.6, -37.08) * mm});
            skLineSegment(sketch, "E388", {"start": v(-228.6, -37.08) * mm, "end": v(-228.6, -21.04) * mm});
            skLineSegment(sketch, "E389", {"start": v(-223.84, -21.04) * mm, "end": v(-228.6, -21.04) * mm});
            skLineSegment(sketch, "E390", {"start": v(-223.84, -21.04) * mm, "end": v(-223.84, -9.76) * mm});
            skLineSegment(sketch, "E391", {"start": v(223.84, -305.04) * mm, "end": v(223.84, -293.76) * mm});
            skLineSegment(sketch, "E392", {"start": v(228.6, -293.76) * mm, "end": v(223.84, -293.76) * mm});
            skLineSegment(sketch, "E393", {"start": v(228.6, -293.76) * mm, "end": v(228.6, -277.72) * mm});
            skLineSegment(sketch, "E394", {"start": v(228.6, -277.72) * mm, "end": v(223.84, -277.72) * mm});
            skLineSegment(sketch, "E395", {"start": v(223.84, -277.72) * mm, "end": v(223.84, -261.68) * mm});
            skLineSegment(sketch, "E396", {"start": v(228.6, -261.68) * mm, "end": v(223.84, -261.68) * mm});
            skLineSegment(sketch, "E397", {"start": v(228.6, -261.68) * mm, "end": v(228.6, -245.63) * mm});
            skLineSegment(sketch, "E398", {"start": v(228.6, -245.63) * mm, "end": v(223.84, -245.63) * mm});
            skLineSegment(sketch, "E399", {"start": v(223.84, -245.63) * mm, "end": v(223.84, -229.6) * mm});
            skLineSegment(sketch, "E400", {"start": v(228.6, -229.6) * mm, "end": v(223.84, -229.6) * mm});
            skLineSegment(sketch, "E401", {"start": v(228.6, -229.6) * mm, "end": v(228.6, -213.55) * mm});
            skLineSegment(sketch, "E402", {"start": v(228.6, -213.55) * mm, "end": v(223.84, -213.55) * mm});
            skLineSegment(sketch, "E403", {"start": v(223.84, -213.55) * mm, "end": v(223.84, -197.5) * mm});
            skLineSegment(sketch, "E404", {"start": v(228.6, -197.5) * mm, "end": v(223.84, -197.5) * mm});
            skLineSegment(sketch, "E405", {"start": v(228.6, -197.5) * mm, "end": v(228.6, -181.47) * mm});
            skLineSegment(sketch, "E406", {"start": v(228.6, -181.47) * mm, "end": v(223.84, -181.47) * mm});
            skLineSegment(sketch, "E407", {"start": v(223.84, -181.47) * mm, "end": v(223.84, -165.42) * mm});
            skLineSegment(sketch, "E408", {"start": v(228.6, -165.42) * mm, "end": v(223.84, -165.42) * mm});
            skLineSegment(sketch, "E409", {"start": v(228.6, -165.42) * mm, "end": v(228.6, -149.38) * mm});
            skLineSegment(sketch, "E410", {"start": v(228.6, -149.38) * mm, "end": v(223.84, -149.38) * mm});
            skLineSegment(sketch, "E411", {"start": v(223.84, -149.38) * mm, "end": v(223.84, -133.34) * mm});
            skLineSegment(sketch, "E412", {"start": v(228.6, -133.34) * mm, "end": v(223.84, -133.34) * mm});
            skLineSegment(sketch, "E413", {"start": v(228.6, -133.34) * mm, "end": v(228.6, -117.3) * mm});
            skLineSegment(sketch, "E414", {"start": v(228.6, -117.3) * mm, "end": v(223.84, -117.3) * mm});
            skLineSegment(sketch, "E415", {"start": v(223.84, -117.3) * mm, "end": v(223.84, -101.25) * mm});
            skLineSegment(sketch, "E416", {"start": v(228.6, -101.25) * mm, "end": v(223.84, -101.25) * mm});
            skLineSegment(sketch, "E417", {"start": v(228.6, -101.25) * mm, "end": v(228.6, -85.21) * mm});
            skLineSegment(sketch, "E418", {"start": v(228.6, -85.21) * mm, "end": v(223.84, -85.21) * mm});
            skLineSegment(sketch, "E419", {"start": v(223.84, -85.21) * mm, "end": v(223.84, -69.17) * mm});
            skLineSegment(sketch, "E420", {"start": v(228.6, -69.17) * mm, "end": v(223.84, -69.17) * mm});
            skLineSegment(sketch, "E421", {"start": v(228.6, -69.17) * mm, "end": v(228.6, -53.13) * mm});
            skLineSegment(sketch, "E422", {"start": v(228.6, -53.13) * mm, "end": v(223.84, -53.13) * mm});
            skLineSegment(sketch, "E423", {"start": v(223.84, -53.13) * mm, "end": v(223.84, -37.08) * mm});
            skLineSegment(sketch, "E424", {"start": v(228.6, -37.08) * mm, "end": v(223.84, -37.08) * mm});
            skLineSegment(sketch, "E425", {"start": v(228.6, -37.08) * mm, "end": v(228.6, -21.04) * mm});
            skLineSegment(sketch, "E426", {"start": v(228.6, -21.04) * mm, "end": v(223.84, -21.04) * mm});
            skLineSegment(sketch, "E427", {"start": v(223.84, -21.04) * mm, "end": v(223.84, -9.76) * mm});
            skLineSegment(sketch, "E428", {"start": v(238.6, -309.8) * mm, "end": v(254.64, -309.8) * mm});
            skLineSegment(sketch, "E429", {"start": v(254.64, -305.04) * mm, "end": v(254.64, -309.8) * mm});
            skLineSegment(sketch, "E430", {"start": v(254.64, -305.04) * mm, "end": v(270.69, -305.04) * mm});
            skLineSegment(sketch, "E431", {"start": v(270.69, -305.04) * mm, "end": v(270.69, -309.8) * mm});
            skLineSegment(sketch, "E432", {"start": v(270.69, -309.8) * mm, "end": v(286.73, -309.8) * mm});
            skLineSegment(sketch, "E433", {"start": v(286.73, -305.04) * mm, "end": v(286.73, -309.8) * mm});
            skLineSegment(sketch, "E434", {"start": v(286.73, -305.04) * mm, "end": v(302.77, -305.04) * mm});
            skLineSegment(sketch, "E435", {"start": v(302.77, -305.04) * mm, "end": v(302.77, -309.8) * mm});
            skLineSegment(sketch, "E436", {"start": v(302.77, -309.8) * mm, "end": v(318.81, -309.8) * mm});
            skLineSegment(sketch, "E437", {"start": v(318.81, -305.04) * mm, "end": v(318.81, -309.8) * mm});
            skLineSegment(sketch, "E438", {"start": v(318.81, -305.04) * mm, "end": v(334.85, -305.04) * mm});
            skLineSegment(sketch, "E439", {"start": v(334.85, -305.04) * mm, "end": v(334.85, -309.8) * mm});
            skLineSegment(sketch, "E440", {"start": v(334.85, -309.8) * mm, "end": v(350.9, -309.8) * mm});
            skLineSegment(sketch, "E441", {"start": v(350.9, -305.04) * mm, "end": v(350.9, -309.8) * mm});
            skLineSegment(sketch, "E442", {"start": v(350.9, -305.04) * mm, "end": v(366.94, -305.04) * mm});
            skLineSegment(sketch, "E443", {"start": v(366.94, -305.04) * mm, "end": v(366.94, -309.8) * mm});
            skLineSegment(sketch, "E444", {"start": v(366.94, -309.8) * mm, "end": v(382.98, -309.8) * mm});
            skLineSegment(sketch, "E445", {"start": v(382.98, -305.04) * mm, "end": v(382.98, -309.8) * mm});
            skLineSegment(sketch, "E446", {"start": v(382.98, -305.04) * mm, "end": v(399.02, -305.04) * mm});
            skLineSegment(sketch, "E447", {"start": v(399.02, -305.04) * mm, "end": v(399.02, -309.8) * mm});
            skLineSegment(sketch, "E448", {"start": v(399.02, -309.8) * mm, "end": v(415.06, -309.8) * mm});
            skLineSegment(sketch, "E449", {"start": v(415.06, -305.04) * mm, "end": v(415.06, -309.8) * mm});
            skLineSegment(sketch, "E450", {"start": v(415.06, -305.04) * mm, "end": v(431.1, -305.04) * mm});
            skLineSegment(sketch, "E451", {"start": v(431.1, -305.04) * mm, "end": v(431.1, -309.8) * mm});
            skLineSegment(sketch, "E452", {"start": v(431.1, -309.8) * mm, "end": v(447.15, -309.8) * mm});
            skLineSegment(sketch, "E453", {"start": v(447.15, -305.04) * mm, "end": v(447.15, -309.8) * mm});
            skLineSegment(sketch, "E454", {"start": v(447.15, -305.04) * mm, "end": v(463.19, -305.04) * mm});
            skLineSegment(sketch, "E455", {"start": v(463.19, -305.04) * mm, "end": v(463.19, -309.8) * mm});
            skLineSegment(sketch, "E456", {"start": v(463.19, -309.8) * mm, "end": v(479.23, -309.8) * mm});
            skLineSegment(sketch, "E457", {"start": v(479.23, -305.04) * mm, "end": v(479.23, -309.8) * mm});
            skLineSegment(sketch, "E458", {"start": v(479.23, -305.04) * mm, "end": v(495.27, -305.04) * mm});
            skLineSegment(sketch, "E459", {"start": v(495.27, -305.04) * mm, "end": v(495.27, -309.8) * mm});
            skLineSegment(sketch, "E460", {"start": v(495.27, -309.8) * mm, "end": v(511.31, -309.8) * mm});
            skLineSegment(sketch, "E461", {"start": v(511.31, -305.04) * mm, "end": v(511.31, -309.8) * mm});
            skLineSegment(sketch, "E462", {"start": v(511.31, -305.04) * mm, "end": v(527.36, -305.04) * mm});
            skLineSegment(sketch, "E463", {"start": v(527.36, -305.04) * mm, "end": v(527.36, -309.8) * mm});
            skLineSegment(sketch, "E464", {"start": v(527.36, -309.8) * mm, "end": v(538.64, -309.8) * mm});
            skLineSegment(sketch, "E465", {"start": v(238.6, -195.5) * mm, "end": v(254.64, -195.5) * mm});
            skLineSegment(sketch, "E466", {"start": v(254.64, -195.5) * mm, "end": v(254.64, -200.26) * mm});
            skLineSegment(sketch, "E467", {"start": v(254.64, -200.26) * mm, "end": v(270.69, -200.26) * mm});
            skLineSegment(sketch, "E468", {"start": v(270.69, -195.5) * mm, "end": v(270.69, -200.26) * mm});
            skLineSegment(sketch, "E469", {"start": v(270.69, -195.5) * mm, "end": v(286.73, -195.5) * mm});
            skLineSegment(sketch, "E470", {"start": v(286.73, -195.5) * mm, "end": v(286.73, -200.26) * mm});
            skLineSegment(sketch, "E471", {"start": v(286.73, -200.26) * mm, "end": v(302.77, -200.26) * mm});
            skLineSegment(sketch, "E472", {"start": v(302.77, -195.5) * mm, "end": v(302.77, -200.26) * mm});
            skLineSegment(sketch, "E473", {"start": v(302.77, -195.5) * mm, "end": v(318.81, -195.5) * mm});
            skLineSegment(sketch, "E474", {"start": v(318.81, -195.5) * mm, "end": v(318.81, -200.26) * mm});
            skLineSegment(sketch, "E475", {"start": v(318.81, -200.26) * mm, "end": v(334.85, -200.26) * mm});
            skLineSegment(sketch, "E476", {"start": v(334.85, -195.5) * mm, "end": v(334.85, -200.26) * mm});
            skLineSegment(sketch, "E477", {"start": v(334.85, -195.5) * mm, "end": v(350.9, -195.5) * mm});
            skLineSegment(sketch, "E478", {"start": v(350.9, -195.5) * mm, "end": v(350.9, -200.26) * mm});
            skLineSegment(sketch, "E479", {"start": v(350.9, -200.26) * mm, "end": v(366.94, -200.26) * mm});
            skLineSegment(sketch, "E480", {"start": v(366.94, -195.5) * mm, "end": v(366.94, -200.26) * mm});
            skLineSegment(sketch, "E481", {"start": v(366.94, -195.5) * mm, "end": v(382.98, -195.5) * mm});
            skLineSegment(sketch, "E482", {"start": v(382.98, -195.5) * mm, "end": v(382.98, -200.26) * mm});
            skLineSegment(sketch, "E483", {"start": v(382.98, -200.26) * mm, "end": v(399.02, -200.26) * mm});
            skLineSegment(sketch, "E484", {"start": v(399.02, -195.5) * mm, "end": v(399.02, -200.26) * mm});
            skLineSegment(sketch, "E485", {"start": v(399.02, -195.5) * mm, "end": v(415.06, -195.5) * mm});
            skLineSegment(sketch, "E486", {"start": v(415.06, -195.5) * mm, "end": v(415.06, -200.26) * mm});
            skLineSegment(sketch, "E487", {"start": v(415.06, -200.26) * mm, "end": v(431.1, -200.26) * mm});
            skLineSegment(sketch, "E488", {"start": v(431.1, -195.5) * mm, "end": v(431.1, -200.26) * mm});
            skLineSegment(sketch, "E489", {"start": v(431.1, -195.5) * mm, "end": v(447.15, -195.5) * mm});
            skLineSegment(sketch, "E490", {"start": v(447.15, -195.5) * mm, "end": v(447.15, -200.26) * mm});
            skLineSegment(sketch, "E491", {"start": v(447.15, -200.26) * mm, "end": v(463.19, -200.26) * mm});
            skLineSegment(sketch, "E492", {"start": v(463.19, -195.5) * mm, "end": v(463.19, -200.26) * mm});
            skLineSegment(sketch, "E493", {"start": v(463.19, -195.5) * mm, "end": v(479.23, -195.5) * mm});
            skLineSegment(sketch, "E494", {"start": v(479.23, -195.5) * mm, "end": v(479.23, -200.26) * mm});
            skLineSegment(sketch, "E495", {"start": v(479.23, -200.26) * mm, "end": v(495.27, -200.26) * mm});
            skLineSegment(sketch, "E496", {"start": v(495.27, -195.5) * mm, "end": v(495.27, -200.26) * mm});
            skLineSegment(sketch, "E497", {"start": v(495.27, -195.5) * mm, "end": v(511.31, -195.5) * mm});
            skLineSegment(sketch, "E498", {"start": v(511.31, -195.5) * mm, "end": v(511.31, -200.26) * mm});
            skLineSegment(sketch, "E499", {"start": v(511.31, -200.26) * mm, "end": v(527.36, -200.26) * mm});
            skLineSegment(sketch, "E500", {"start": v(527.36, -195.5) * mm, "end": v(527.36, -200.26) * mm});
            skLineSegment(sketch, "E501", {"start": v(527.36, -195.5) * mm, "end": v(538.64, -195.5) * mm});
            skLineSegment(sketch, "E502", {"start": v(238.6, -309.8) * mm, "end": v(238.6, -293.47) * mm});
            skLineSegment(sketch, "E503", {"start": v(243.36, -293.47) * mm, "end": v(238.6, -293.47) * mm});
            skLineSegment(sketch, "E504", {"start": v(243.36, -293.47) * mm, "end": v(243.36, -277.14) * mm});
            skLineSegment(sketch, "E505", {"start": v(243.36, -277.14) * mm, "end": v(238.6, -277.14) * mm});
            skLineSegment(sketch, "E506", {"start": v(238.6, -277.14) * mm, "end": v(238.6, -260.82) * mm});
            skLineSegment(sketch, "E507", {"start": v(243.36, -260.82) * mm, "end": v(238.6, -260.82) * mm});
            skLineSegment(sketch, "E508", {"start": v(243.36, -260.82) * mm, "end": v(243.36, -244.49) * mm});
            skLineSegment(sketch, "E509", {"start": v(243.36, -244.49) * mm, "end": v(238.6, -244.49) * mm});
            skLineSegment(sketch, "E510", {"start": v(238.6, -244.49) * mm, "end": v(238.6, -228.16) * mm});
            skLineSegment(sketch, "E511", {"start": v(243.36, -228.16) * mm, "end": v(238.6, -228.16) * mm});
            skLineSegment(sketch, "E512", {"start": v(243.36, -228.16) * mm, "end": v(243.36, -211.83) * mm});
            skLineSegment(sketch, "E513", {"start": v(243.36, -211.83) * mm, "end": v(238.6, -211.83) * mm});
            skLineSegment(sketch, "E514", {"start": v(238.6, -211.83) * mm, "end": v(238.6, -195.5) * mm});
            skLineSegment(sketch, "E515", {"start": v(538.64, -309.8) * mm, "end": v(538.64, -293.47) * mm});
            skLineSegment(sketch, "E516", {"start": v(543.4, -293.47) * mm, "end": v(538.64, -293.47) * mm});
            skLineSegment(sketch, "E517", {"start": v(543.4, -293.47) * mm, "end": v(543.4, -277.14) * mm});
            skLineSegment(sketch, "E518", {"start": v(543.4, -277.14) * mm, "end": v(538.64, -277.14) * mm});
            skLineSegment(sketch, "E519", {"start": v(538.64, -277.14) * mm, "end": v(538.64, -260.82) * mm});
            skLineSegment(sketch, "E520", {"start": v(543.4, -260.82) * mm, "end": v(538.64, -260.82) * mm});
            skLineSegment(sketch, "E521", {"start": v(543.4, -260.82) * mm, "end": v(543.4, -244.49) * mm});
            skLineSegment(sketch, "E522", {"start": v(543.4, -244.49) * mm, "end": v(538.64, -244.49) * mm});
            skLineSegment(sketch, "E523", {"start": v(538.64, -244.49) * mm, "end": v(538.64, -228.16) * mm});
            skLineSegment(sketch, "E524", {"start": v(543.4, -228.16) * mm, "end": v(538.64, -228.16) * mm});
            skLineSegment(sketch, "E525", {"start": v(543.4, -228.16) * mm, "end": v(543.4, -211.83) * mm});
            skLineSegment(sketch, "E526", {"start": v(543.4, -211.83) * mm, "end": v(538.64, -211.83) * mm});
            skLineSegment(sketch, "E527", {"start": v(538.64, -211.83) * mm, "end": v(538.64, -195.5) * mm});
            skLineSegment(sketch, "E528", {"start": v(-228.6, 5) * mm, "end": v(-212.83, 5) * mm});
            skLineSegment(sketch, "E529", {"start": v(-212.83, 9.76) * mm, "end": v(-212.83, 5) * mm});
            skLineSegment(sketch, "E530", {"start": v(-212.83, 9.76) * mm, "end": v(-197.07, 9.76) * mm});
            skLineSegment(sketch, "E531", {"start": v(-197.07, 9.76) * mm, "end": v(-197.07, 5) * mm});
            skLineSegment(sketch, "E532", {"start": v(-197.07, 5) * mm, "end": v(-181.3, 5) * mm});
            skLineSegment(sketch, "E533", {"start": v(-181.3, 9.76) * mm, "end": v(-181.3, 5) * mm});
            skLineSegment(sketch, "E534", {"start": v(-181.3, 9.76) * mm, "end": v(-165.54, 9.76) * mm});
            skLineSegment(sketch, "E535", {"start": v(-165.54, 9.76) * mm, "end": v(-165.54, 5) * mm});
            skLineSegment(sketch, "E536", {"start": v(-165.54, 5) * mm, "end": v(-149.77, 5) * mm});
            skLineSegment(sketch, "E537", {"start": v(-149.77, 9.76) * mm, "end": v(-149.77, 5) * mm});
            skLineSegment(sketch, "E538", {"start": v(-149.77, 9.76) * mm, "end": v(-134, 9.76) * mm});
            skLineSegment(sketch, "E539", {"start": v(-134, 9.76) * mm, "end": v(-134, 5) * mm});
            skLineSegment(sketch, "E540", {"start": v(-134, 5) * mm, "end": v(-118.24, 5) * mm});
            skLineSegment(sketch, "E541", {"start": v(-118.24, 9.76) * mm, "end": v(-118.24, 5) * mm});
            skLineSegment(sketch, "E542", {"start": v(-118.24, 9.76) * mm, "end": v(-102.48, 9.76) * mm});
            skLineSegment(sketch, "E543", {"start": v(-102.48, 9.76) * mm, "end": v(-102.48, 5) * mm});
            skLineSegment(sketch, "E544", {"start": v(-102.48, 5) * mm, "end": v(-86.71, 5) * mm});
            skLineSegment(sketch, "E545", {"start": v(-86.71, 9.76) * mm, "end": v(-86.71, 5) * mm});
            skLineSegment(sketch, "E546", {"start": v(-86.71, 9.76) * mm, "end": v(-70.94, 9.76) * mm});
            skLineSegment(sketch, "E547", {"start": v(-70.94, 9.76) * mm, "end": v(-70.94, 5) * mm});
            skLineSegment(sketch, "E548", {"start": v(-70.94, 5) * mm, "end": v(-55.18, 5) * mm});
            skLineSegment(sketch, "E549", {"start": v(-55.18, 9.76) * mm, "end": v(-55.18, 5) * mm});
            skLineSegment(sketch, "E550", {"start": v(-55.18, 9.76) * mm, "end": v(-39.41, 9.76) * mm});
            skLineSegment(sketch, "E551", {"start": v(-39.41, 9.76) * mm, "end": v(-39.41, 5) * mm});
            skLineSegment(sketch, "E552", {"start": v(-39.41, 5) * mm, "end": v(-23.65, 5) * mm});
            skLineSegment(sketch, "E553", {"start": v(-23.65, 9.76) * mm, "end": v(-23.65, 5) * mm});
            skLineSegment(sketch, "E554", {"start": v(-23.65, 9.76) * mm, "end": v(-7.88, 9.76) * mm});
            skLineSegment(sketch, "E555", {"start": v(-7.88, 9.76) * mm, "end": v(-7.88, 5) * mm});
            skLineSegment(sketch, "E556", {"start": v(-7.88, 5) * mm, "end": v(7.88, 5) * mm});
            skLineSegment(sketch, "E557", {"start": v(7.88, 9.76) * mm, "end": v(7.88, 5) * mm});
            skLineSegment(sketch, "E558", {"start": v(7.88, 9.76) * mm, "end": v(23.65, 9.76) * mm});
            skLineSegment(sketch, "E559", {"start": v(23.65, 9.76) * mm, "end": v(23.65, 5) * mm});
            skLineSegment(sketch, "E560", {"start": v(23.65, 5) * mm, "end": v(39.42, 5) * mm});
            skLineSegment(sketch, "E561", {"start": v(39.42, 9.76) * mm, "end": v(39.42, 5) * mm});
            skLineSegment(sketch, "E562", {"start": v(39.42, 9.76) * mm, "end": v(55.18, 9.76) * mm});
            skLineSegment(sketch, "E563", {"start": v(55.18, 9.76) * mm, "end": v(55.18, 5) * mm});
            skLineSegment(sketch, "E564", {"start": v(55.18, 5) * mm, "end": v(70.95, 5) * mm});
            skLineSegment(sketch, "E565", {"start": v(70.95, 9.76) * mm, "end": v(70.95, 5) * mm});
            skLineSegment(sketch, "E566", {"start": v(70.95, 9.76) * mm, "end": v(86.7, 9.76) * mm});
            skLineSegment(sketch, "E567", {"start": v(86.7, 9.76) * mm, "end": v(86.7, 5) * mm});
            skLineSegment(sketch, "E568", {"start": v(86.7, 5) * mm, "end": v(102.48, 5) * mm});
            skLineSegment(sketch, "E569", {"start": v(102.48, 9.76) * mm, "end": v(102.48, 5) * mm});
            skLineSegment(sketch, "E570", {"start": v(102.48, 9.76) * mm, "end": v(118.24, 9.76) * mm});
            skLineSegment(sketch, "E571", {"start": v(118.24, 9.76) * mm, "end": v(118.24, 5) * mm});
            skLineSegment(sketch, "E572", {"start": v(118.24, 5) * mm, "end": v(134, 5) * mm});
            skLineSegment(sketch, "E573", {"start": v(134, 9.76) * mm, "end": v(134, 5) * mm});
            skLineSegment(sketch, "E574", {"start": v(134, 9.76) * mm, "end": v(149.77, 9.76) * mm});
            skLineSegment(sketch, "E575", {"start": v(149.77, 9.76) * mm, "end": v(149.77, 5) * mm});
            skLineSegment(sketch, "E576", {"start": v(149.77, 5) * mm, "end": v(165.54, 5) * mm});
            skLineSegment(sketch, "E577", {"start": v(165.54, 9.76) * mm, "end": v(165.54, 5) * mm});
            skLineSegment(sketch, "E578", {"start": v(165.54, 9.76) * mm, "end": v(181.3, 9.76) * mm});
            skLineSegment(sketch, "E579", {"start": v(181.3, 9.76) * mm, "end": v(181.3, 5) * mm});
            skLineSegment(sketch, "E580", {"start": v(181.3, 5) * mm, "end": v(197.07, 5) * mm});
            skLineSegment(sketch, "E581", {"start": v(197.07, 9.76) * mm, "end": v(197.07, 5) * mm});
            skLineSegment(sketch, "E582", {"start": v(197.07, 9.76) * mm, "end": v(212.83, 9.76) * mm});
            skLineSegment(sketch, "E583", {"start": v(212.83, 9.76) * mm, "end": v(212.83, 5) * mm});
            skLineSegment(sketch, "E584", {"start": v(212.83, 5) * mm, "end": v(223.84, 5) * mm});
            skLineSegment(sketch, "E585", {"start": v(-228.6, 119.3) * mm, "end": v(-212.83, 119.3) * mm});
            skLineSegment(sketch, "E586", {"start": v(-212.83, 119.3) * mm, "end": v(-212.83, 114.54) * mm});
            skLineSegment(sketch, "E587", {"start": v(-212.83, 114.54) * mm, "end": v(-197.07, 114.54) * mm});
            skLineSegment(sketch, "E588", {"start": v(-197.07, 119.3) * mm, "end": v(-197.07, 114.54) * mm});
            skLineSegment(sketch, "E589", {"start": v(-197.07, 119.3) * mm, "end": v(-181.3, 119.3) * mm});
            skLineSegment(sketch, "E590", {"start": v(-181.3, 119.3) * mm, "end": v(-181.3, 114.54) * mm});
            skLineSegment(sketch, "E591", {"start": v(-181.3, 114.54) * mm, "end": v(-165.54, 114.54) * mm});
            skLineSegment(sketch, "E592", {"start": v(-165.54, 119.3) * mm, "end": v(-165.54, 114.54) * mm});
            skLineSegment(sketch, "E593", {"start": v(-165.54, 119.3) * mm, "end": v(-149.77, 119.3) * mm});
            skLineSegment(sketch, "E594", {"start": v(-149.77, 119.3) * mm, "end": v(-149.77, 114.54) * mm});
            skLineSegment(sketch, "E595", {"start": v(-149.77, 114.54) * mm, "end": v(-134, 114.54) * mm});
            skLineSegment(sketch, "E596", {"start": v(-134, 119.3) * mm, "end": v(-134, 114.54) * mm});
            skLineSegment(sketch, "E597", {"start": v(-134, 119.3) * mm, "end": v(-118.24, 119.3) * mm});
            skLineSegment(sketch, "E598", {"start": v(-118.24, 119.3) * mm, "end": v(-118.24, 114.54) * mm});
            skLineSegment(sketch, "E599", {"start": v(-118.24, 114.54) * mm, "end": v(-102.48, 114.54) * mm});
            skLineSegment(sketch, "E600", {"start": v(-102.48, 119.3) * mm, "end": v(-102.48, 114.54) * mm});
            skLineSegment(sketch, "E601", {"start": v(-102.48, 119.3) * mm, "end": v(-86.71, 119.3) * mm});
            skLineSegment(sketch, "E602", {"start": v(-86.71, 119.3) * mm, "end": v(-86.71, 114.54) * mm});
            skLineSegment(sketch, "E603", {"start": v(-86.71, 114.54) * mm, "end": v(-70.94, 114.54) * mm});
            skLineSegment(sketch, "E604", {"start": v(-70.94, 119.3) * mm, "end": v(-70.94, 114.54) * mm});
            skLineSegment(sketch, "E605", {"start": v(-70.94, 119.3) * mm, "end": v(-55.18, 119.3) * mm});
            skLineSegment(sketch, "E606", {"start": v(-55.18, 119.3) * mm, "end": v(-55.18, 114.54) * mm});
            skLineSegment(sketch, "E607", {"start": v(-55.18, 114.54) * mm, "end": v(-39.41, 114.54) * mm});
            skLineSegment(sketch, "E608", {"start": v(-39.41, 119.3) * mm, "end": v(-39.41, 114.54) * mm});
            skLineSegment(sketch, "E609", {"start": v(-39.41, 119.3) * mm, "end": v(-23.65, 119.3) * mm});
            skLineSegment(sketch, "E610", {"start": v(-23.65, 119.3) * mm, "end": v(-23.65, 114.54) * mm});
            skLineSegment(sketch, "E611", {"start": v(-23.65, 114.54) * mm, "end": v(-7.88, 114.54) * mm});
            skLineSegment(sketch, "E612", {"start": v(-7.88, 119.3) * mm, "end": v(-7.88, 114.54) * mm});
            skLineSegment(sketch, "E613", {"start": v(-7.88, 119.3) * mm, "end": v(7.88, 119.3) * mm});
            skLineSegment(sketch, "E614", {"start": v(7.88, 119.3) * mm, "end": v(7.88, 114.54) * mm});
            skLineSegment(sketch, "E615", {"start": v(7.88, 114.54) * mm, "end": v(23.65, 114.54) * mm});
            skLineSegment(sketch, "E616", {"start": v(23.65, 119.3) * mm, "end": v(23.65, 114.54) * mm});
            skLineSegment(sketch, "E617", {"start": v(23.65, 119.3) * mm, "end": v(39.42, 119.3) * mm});
            skLineSegment(sketch, "E618", {"start": v(39.42, 119.3) * mm, "end": v(39.42, 114.54) * mm});
            skLineSegment(sketch, "E619", {"start": v(39.42, 114.54) * mm, "end": v(55.18, 114.54) * mm});
            skLineSegment(sketch, "E620", {"start": v(55.18, 119.3) * mm, "end": v(55.18, 114.54) * mm});
            skLineSegment(sketch, "E621", {"start": v(55.18, 119.3) * mm, "end": v(70.95, 119.3) * mm});
            skLineSegment(sketch, "E622", {"start": v(70.95, 119.3) * mm, "end": v(70.95, 114.54) * mm});
            skLineSegment(sketch, "E623", {"start": v(70.95, 114.54) * mm, "end": v(86.7, 114.54) * mm});
            skLineSegment(sketch, "E624", {"start": v(86.7, 119.3) * mm, "end": v(86.7, 114.54) * mm});
            skLineSegment(sketch, "E625", {"start": v(86.7, 119.3) * mm, "end": v(102.48, 119.3) * mm});
            skLineSegment(sketch, "E626", {"start": v(102.48, 119.3) * mm, "end": v(102.48, 114.54) * mm});
            skLineSegment(sketch, "E627", {"start": v(102.48, 114.54) * mm, "end": v(118.24, 114.54) * mm});
            skLineSegment(sketch, "E628", {"start": v(118.24, 119.3) * mm, "end": v(118.24, 114.54) * mm});
            skLineSegment(sketch, "E629", {"start": v(118.24, 119.3) * mm, "end": v(134, 119.3) * mm});
            skLineSegment(sketch, "E630", {"start": v(134, 119.3) * mm, "end": v(134, 114.54) * mm});
            skLineSegment(sketch, "E631", {"start": v(134, 114.54) * mm, "end": v(149.77, 114.54) * mm});
            skLineSegment(sketch, "E632", {"start": v(149.77, 119.3) * mm, "end": v(149.77, 114.54) * mm});
            skLineSegment(sketch, "E633", {"start": v(149.77, 119.3) * mm, "end": v(165.54, 119.3) * mm});
            skLineSegment(sketch, "E634", {"start": v(165.54, 119.3) * mm, "end": v(165.54, 114.54) * mm});
            skLineSegment(sketch, "E635", {"start": v(165.54, 114.54) * mm, "end": v(181.3, 114.54) * mm});
            skLineSegment(sketch, "E636", {"start": v(181.3, 119.3) * mm, "end": v(181.3, 114.54) * mm});
            skLineSegment(sketch, "E637", {"start": v(181.3, 119.3) * mm, "end": v(197.07, 119.3) * mm});
            skLineSegment(sketch, "E638", {"start": v(197.07, 119.3) * mm, "end": v(197.07, 114.54) * mm});
            skLineSegment(sketch, "E639", {"start": v(197.07, 114.54) * mm, "end": v(212.83, 114.54) * mm});
            skLineSegment(sketch, "E640", {"start": v(212.83, 119.3) * mm, "end": v(212.83, 114.54) * mm});
            skLineSegment(sketch, "E641", {"start": v(212.83, 119.3) * mm, "end": v(223.84, 119.3) * mm});
            skLineSegment(sketch, "E642", {"start": v(-228.6, 5) * mm, "end": v(-228.6, 21.33) * mm});
            skLineSegment(sketch, "E643", {"start": v(-223.84, 21.33) * mm, "end": v(-228.6, 21.33) * mm});
            skLineSegment(sketch, "E644", {"start": v(-223.84, 21.33) * mm, "end": v(-223.84, 37.66) * mm});
            skLineSegment(sketch, "E645", {"start": v(-223.84, 37.66) * mm, "end": v(-228.6, 37.66) * mm});
            skLineSegment(sketch, "E646", {"start": v(-228.6, 37.66) * mm, "end": v(-228.6, 53.98) * mm});
            skLineSegment(sketch, "E647", {"start": v(-223.84, 53.98) * mm, "end": v(-228.6, 53.98) * mm});
            skLineSegment(sketch, "E648", {"start": v(-223.84, 53.98) * mm, "end": v(-223.84, 70.31) * mm});
            skLineSegment(sketch, "E649", {"start": v(-223.84, 70.31) * mm, "end": v(-228.6, 70.31) * mm});
            skLineSegment(sketch, "E650", {"start": v(-228.6, 70.31) * mm, "end": v(-228.6, 86.64) * mm});
            skLineSegment(sketch, "E651", {"start": v(-223.84, 86.64) * mm, "end": v(-228.6, 86.64) * mm});
            skLineSegment(sketch, "E652", {"start": v(-223.84, 86.64) * mm, "end": v(-223.84, 102.97) * mm});
            skLineSegment(sketch, "E653", {"start": v(-223.84, 102.97) * mm, "end": v(-228.6, 102.97) * mm});
            skLineSegment(sketch, "E654", {"start": v(-228.6, 102.97) * mm, "end": v(-228.6, 119.3) * mm});
            skLineSegment(sketch, "E655", {"start": v(223.84, 5) * mm, "end": v(223.84, 21.33) * mm});
            skLineSegment(sketch, "E656", {"start": v(228.6, 21.33) * mm, "end": v(223.84, 21.33) * mm});
            skLineSegment(sketch, "E657", {"start": v(228.6, 21.33) * mm, "end": v(228.6, 37.66) * mm});
            skLineSegment(sketch, "E658", {"start": v(228.6, 37.66) * mm, "end": v(223.84, 37.66) * mm});
            skLineSegment(sketch, "E659", {"start": v(223.84, 37.66) * mm, "end": v(223.84, 53.98) * mm});
            skLineSegment(sketch, "E660", {"start": v(228.6, 53.98) * mm, "end": v(223.84, 53.98) * mm});
            skLineSegment(sketch, "E661", {"start": v(228.6, 53.98) * mm, "end": v(228.6, 70.31) * mm});
            skLineSegment(sketch, "E662", {"start": v(228.6, 70.31) * mm, "end": v(223.84, 70.31) * mm});
            skLineSegment(sketch, "E663", {"start": v(223.84, 70.31) * mm, "end": v(223.84, 86.64) * mm});
            skLineSegment(sketch, "E664", {"start": v(228.6, 86.64) * mm, "end": v(223.84, 86.64) * mm});
            skLineSegment(sketch, "E665", {"start": v(228.6, 86.64) * mm, "end": v(228.6, 102.97) * mm});
            skLineSegment(sketch, "E666", {"start": v(228.6, 102.97) * mm, "end": v(223.84, 102.97) * mm});
            skLineSegment(sketch, "E667", {"start": v(223.84, 102.97) * mm, "end": v(223.84, 119.3) * mm});
            skLineSegment(sketch, "E668", {"start": v(-223.84, 134.06) * mm, "end": v(-212.83, 134.06) * mm});
            skLineSegment(sketch, "E669", {"start": v(-212.83, 134.06) * mm, "end": v(-212.83, 129.3) * mm});
            skLineSegment(sketch, "E670", {"start": v(-212.83, 129.3) * mm, "end": v(-197.07, 129.3) * mm});
            skLineSegment(sketch, "E671", {"start": v(-197.07, 134.06) * mm, "end": v(-197.07, 129.3) * mm});
            skLineSegment(sketch, "E672", {"start": v(-197.07, 134.06) * mm, "end": v(-181.3, 134.06) * mm});
            skLineSegment(sketch, "E673", {"start": v(-181.3, 134.06) * mm, "end": v(-181.3, 129.3) * mm});
            skLineSegment(sketch, "E674", {"start": v(-181.3, 129.3) * mm, "end": v(-165.54, 129.3) * mm});
            skLineSegment(sketch, "E675", {"start": v(-165.54, 134.06) * mm, "end": v(-165.54, 129.3) * mm});
            skLineSegment(sketch, "E676", {"start": v(-165.54, 134.06) * mm, "end": v(-149.77, 134.06) * mm});
            skLineSegment(sketch, "E677", {"start": v(-149.77, 134.06) * mm, "end": v(-149.77, 129.3) * mm});
            skLineSegment(sketch, "E678", {"start": v(-149.77, 129.3) * mm, "end": v(-134, 129.3) * mm});
            skLineSegment(sketch, "E679", {"start": v(-134, 134.06) * mm, "end": v(-134, 129.3) * mm});
            skLineSegment(sketch, "E680", {"start": v(-134, 134.06) * mm, "end": v(-118.24, 134.06) * mm});
            skLineSegment(sketch, "E681", {"start": v(-118.24, 134.06) * mm, "end": v(-118.24, 129.3) * mm});
            skLineSegment(sketch, "E682", {"start": v(-118.24, 129.3) * mm, "end": v(-102.48, 129.3) * mm});
            skLineSegment(sketch, "E683", {"start": v(-102.48, 134.06) * mm, "end": v(-102.48, 129.3) * mm});
            skLineSegment(sketch, "E684", {"start": v(-102.48, 134.06) * mm, "end": v(-86.71, 134.06) * mm});
            skLineSegment(sketch, "E685", {"start": v(-86.71, 134.06) * mm, "end": v(-86.71, 129.3) * mm});
            skLineSegment(sketch, "E686", {"start": v(-86.71, 129.3) * mm, "end": v(-70.94, 129.3) * mm});
            skLineSegment(sketch, "E687", {"start": v(-70.94, 134.06) * mm, "end": v(-70.94, 129.3) * mm});
            skLineSegment(sketch, "E688", {"start": v(-70.94, 134.06) * mm, "end": v(-55.18, 134.06) * mm});
            skLineSegment(sketch, "E689", {"start": v(-55.18, 134.06) * mm, "end": v(-55.18, 129.3) * mm});
            skLineSegment(sketch, "E690", {"start": v(-55.18, 129.3) * mm, "end": v(-39.41, 129.3) * mm});
            skLineSegment(sketch, "E691", {"start": v(-39.41, 134.06) * mm, "end": v(-39.41, 129.3) * mm});
            skLineSegment(sketch, "E692", {"start": v(-39.41, 134.06) * mm, "end": v(-23.65, 134.06) * mm});
            skLineSegment(sketch, "E693", {"start": v(-23.65, 134.06) * mm, "end": v(-23.65, 129.3) * mm});
            skLineSegment(sketch, "E694", {"start": v(-23.65, 129.3) * mm, "end": v(-7.88, 129.3) * mm});
            skLineSegment(sketch, "E695", {"start": v(-7.88, 134.06) * mm, "end": v(-7.88, 129.3) * mm});
            skLineSegment(sketch, "E696", {"start": v(-7.88, 134.06) * mm, "end": v(7.88, 134.06) * mm});
            skLineSegment(sketch, "E697", {"start": v(7.88, 134.06) * mm, "end": v(7.88, 129.3) * mm});
            skLineSegment(sketch, "E698", {"start": v(7.88, 129.3) * mm, "end": v(23.65, 129.3) * mm});
            skLineSegment(sketch, "E699", {"start": v(23.65, 134.06) * mm, "end": v(23.65, 129.3) * mm});
            skLineSegment(sketch, "E700", {"start": v(23.65, 134.06) * mm, "end": v(39.42, 134.06) * mm});
            skLineSegment(sketch, "E701", {"start": v(39.42, 134.06) * mm, "end": v(39.42, 129.3) * mm});
            skLineSegment(sketch, "E702", {"start": v(39.42, 129.3) * mm, "end": v(55.18, 129.3) * mm});
            skLineSegment(sketch, "E703", {"start": v(55.18, 134.06) * mm, "end": v(55.18, 129.3) * mm});
            skLineSegment(sketch, "E704", {"start": v(55.18, 134.06) * mm, "end": v(70.95, 134.06) * mm});
            skLineSegment(sketch, "E705", {"start": v(70.95, 134.06) * mm, "end": v(70.95, 129.3) * mm});
            skLineSegment(sketch, "E706", {"start": v(70.95, 129.3) * mm, "end": v(86.7, 129.3) * mm});
            skLineSegment(sketch, "E707", {"start": v(86.7, 134.06) * mm, "end": v(86.7, 129.3) * mm});
            skLineSegment(sketch, "E708", {"start": v(86.7, 134.06) * mm, "end": v(102.48, 134.06) * mm});
            skLineSegment(sketch, "E709", {"start": v(102.48, 134.06) * mm, "end": v(102.48, 129.3) * mm});
            skLineSegment(sketch, "E710", {"start": v(102.48, 129.3) * mm, "end": v(118.24, 129.3) * mm});
            skLineSegment(sketch, "E711", {"start": v(118.24, 134.06) * mm, "end": v(118.24, 129.3) * mm});
            skLineSegment(sketch, "E712", {"start": v(118.24, 134.06) * mm, "end": v(134, 134.06) * mm});
            skLineSegment(sketch, "E713", {"start": v(134, 134.06) * mm, "end": v(134, 129.3) * mm});
            skLineSegment(sketch, "E714", {"start": v(134, 129.3) * mm, "end": v(149.77, 129.3) * mm});
            skLineSegment(sketch, "E715", {"start": v(149.77, 134.06) * mm, "end": v(149.77, 129.3) * mm});
            skLineSegment(sketch, "E716", {"start": v(149.77, 134.06) * mm, "end": v(165.54, 134.06) * mm});
            skLineSegment(sketch, "E717", {"start": v(165.54, 134.06) * mm, "end": v(165.54, 129.3) * mm});
            skLineSegment(sketch, "E718", {"start": v(165.54, 129.3) * mm, "end": v(181.3, 129.3) * mm});
            skLineSegment(sketch, "E719", {"start": v(181.3, 134.06) * mm, "end": v(181.3, 129.3) * mm});
            skLineSegment(sketch, "E720", {"start": v(181.3, 134.06) * mm, "end": v(197.07, 134.06) * mm});
            skLineSegment(sketch, "E721", {"start": v(197.07, 134.06) * mm, "end": v(197.07, 129.3) * mm});
            skLineSegment(sketch, "E722", {"start": v(197.07, 129.3) * mm, "end": v(212.83, 129.3) * mm});
            skLineSegment(sketch, "E723", {"start": v(212.83, 134.06) * mm, "end": v(212.83, 129.3) * mm});
            skLineSegment(sketch, "E724", {"start": v(212.83, 134.06) * mm, "end": v(223.84, 134.06) * mm});
            skLineSegment(sketch, "E725", {"start": v(-223.84, 429.34) * mm, "end": v(-212.83, 429.34) * mm});
            skLineSegment(sketch, "E726", {"start": v(-212.83, 434.1) * mm, "end": v(-212.83, 429.34) * mm});
            skLineSegment(sketch, "E727", {"start": v(-212.83, 434.1) * mm, "end": v(-197.07, 434.1) * mm});
            skLineSegment(sketch, "E728", {"start": v(-197.07, 434.1) * mm, "end": v(-197.07, 429.34) * mm});
            skLineSegment(sketch, "E729", {"start": v(-197.07, 429.34) * mm, "end": v(-181.3, 429.34) * mm});
            skLineSegment(sketch, "E730", {"start": v(-181.3, 434.1) * mm, "end": v(-181.3, 429.34) * mm});
            skLineSegment(sketch, "E731", {"start": v(-181.3, 434.1) * mm, "end": v(-165.54, 434.1) * mm});
            skLineSegment(sketch, "E732", {"start": v(-165.54, 434.1) * mm, "end": v(-165.54, 429.34) * mm});
            skLineSegment(sketch, "E733", {"start": v(-165.54, 429.34) * mm, "end": v(-149.77, 429.34) * mm});
            skLineSegment(sketch, "E734", {"start": v(-149.77, 434.1) * mm, "end": v(-149.77, 429.34) * mm});
            skLineSegment(sketch, "E735", {"start": v(-149.77, 434.1) * mm, "end": v(-134, 434.1) * mm});
            skLineSegment(sketch, "E736", {"start": v(-134, 434.1) * mm, "end": v(-134, 429.34) * mm});
            skLineSegment(sketch, "E737", {"start": v(-134, 429.34) * mm, "end": v(-118.24, 429.34) * mm});
            skLineSegment(sketch, "E738", {"start": v(-118.24, 434.1) * mm, "end": v(-118.24, 429.34) * mm});
            skLineSegment(sketch, "E739", {"start": v(-118.24, 434.1) * mm, "end": v(-102.48, 434.1) * mm});
            skLineSegment(sketch, "E740", {"start": v(-102.48, 434.1) * mm, "end": v(-102.48, 429.34) * mm});
            skLineSegment(sketch, "E741", {"start": v(-102.48, 429.34) * mm, "end": v(-86.71, 429.34) * mm});
            skLineSegment(sketch, "E742", {"start": v(-86.71, 434.1) * mm, "end": v(-86.71, 429.34) * mm});
            skLineSegment(sketch, "E743", {"start": v(-86.71, 434.1) * mm, "end": v(-70.94, 434.1) * mm});
            skLineSegment(sketch, "E744", {"start": v(-70.94, 434.1) * mm, "end": v(-70.94, 429.34) * mm});
            skLineSegment(sketch, "E745", {"start": v(-70.94, 429.34) * mm, "end": v(-55.18, 429.34) * mm});
            skLineSegment(sketch, "E746", {"start": v(-55.18, 434.1) * mm, "end": v(-55.18, 429.34) * mm});
            skLineSegment(sketch, "E747", {"start": v(-55.18, 434.1) * mm, "end": v(-39.41, 434.1) * mm});
            skLineSegment(sketch, "E748", {"start": v(-39.41, 434.1) * mm, "end": v(-39.41, 429.34) * mm});
            skLineSegment(sketch, "E749", {"start": v(-39.41, 429.34) * mm, "end": v(-23.65, 429.34) * mm});
            skLineSegment(sketch, "E750", {"start": v(-23.65, 434.1) * mm, "end": v(-23.65, 429.34) * mm});
            skLineSegment(sketch, "E751", {"start": v(-23.65, 434.1) * mm, "end": v(-7.88, 434.1) * mm});
            skLineSegment(sketch, "E752", {"start": v(-7.88, 434.1) * mm, "end": v(-7.88, 429.34) * mm});
            skLineSegment(sketch, "E753", {"start": v(-7.88, 429.34) * mm, "end": v(7.88, 429.34) * mm});
            skLineSegment(sketch, "E754", {"start": v(7.88, 434.1) * mm, "end": v(7.88, 429.34) * mm});
            skLineSegment(sketch, "E755", {"start": v(7.88, 434.1) * mm, "end": v(23.65, 434.1) * mm});
            skLineSegment(sketch, "E756", {"start": v(23.65, 434.1) * mm, "end": v(23.65, 429.34) * mm});
            skLineSegment(sketch, "E757", {"start": v(23.65, 429.34) * mm, "end": v(39.42, 429.34) * mm});
            skLineSegment(sketch, "E758", {"start": v(39.42, 434.1) * mm, "end": v(39.42, 429.34) * mm});
            skLineSegment(sketch, "E759", {"start": v(39.42, 434.1) * mm, "end": v(55.18, 434.1) * mm});
            skLineSegment(sketch, "E760", {"start": v(55.18, 434.1) * mm, "end": v(55.18, 429.34) * mm});
            skLineSegment(sketch, "E761", {"start": v(55.18, 429.34) * mm, "end": v(70.95, 429.34) * mm});
            skLineSegment(sketch, "E762", {"start": v(70.95, 434.1) * mm, "end": v(70.95, 429.34) * mm});
            skLineSegment(sketch, "E763", {"start": v(70.95, 434.1) * mm, "end": v(86.7, 434.1) * mm});
            skLineSegment(sketch, "E764", {"start": v(86.7, 434.1) * mm, "end": v(86.7, 429.34) * mm});
            skLineSegment(sketch, "E765", {"start": v(86.7, 429.34) * mm, "end": v(102.48, 429.34) * mm});
            skLineSegment(sketch, "E766", {"start": v(102.48, 434.1) * mm, "end": v(102.48, 429.34) * mm});
            skLineSegment(sketch, "E767", {"start": v(102.48, 434.1) * mm, "end": v(118.24, 434.1) * mm});
            skLineSegment(sketch, "E768", {"start": v(118.24, 434.1) * mm, "end": v(118.24, 429.34) * mm});
            skLineSegment(sketch, "E769", {"start": v(118.24, 429.34) * mm, "end": v(134, 429.34) * mm});
            skLineSegment(sketch, "E770", {"start": v(134, 434.1) * mm, "end": v(134, 429.34) * mm});
            skLineSegment(sketch, "E771", {"start": v(134, 434.1) * mm, "end": v(149.77, 434.1) * mm});
            skLineSegment(sketch, "E772", {"start": v(149.77, 434.1) * mm, "end": v(149.77, 429.34) * mm});
            skLineSegment(sketch, "E773", {"start": v(149.77, 429.34) * mm, "end": v(165.54, 429.34) * mm});
            skLineSegment(sketch, "E774", {"start": v(165.54, 434.1) * mm, "end": v(165.54, 429.34) * mm});
            skLineSegment(sketch, "E775", {"start": v(165.54, 434.1) * mm, "end": v(181.3, 434.1) * mm});
            skLineSegment(sketch, "E776", {"start": v(181.3, 434.1) * mm, "end": v(181.3, 429.34) * mm});
            skLineSegment(sketch, "E777", {"start": v(181.3, 429.34) * mm, "end": v(197.07, 429.34) * mm});
            skLineSegment(sketch, "E778", {"start": v(197.07, 434.1) * mm, "end": v(197.07, 429.34) * mm});
            skLineSegment(sketch, "E779", {"start": v(197.07, 434.1) * mm, "end": v(212.83, 434.1) * mm});
            skLineSegment(sketch, "E780", {"start": v(212.83, 434.1) * mm, "end": v(212.83, 429.34) * mm});
            skLineSegment(sketch, "E781", {"start": v(212.83, 429.34) * mm, "end": v(223.84, 429.34) * mm});
            skLineSegment(sketch, "E782", {"start": v(-223.84, 134.06) * mm, "end": v(-223.84, 145.34) * mm});
            skLineSegment(sketch, "E783", {"start": v(-223.84, 145.34) * mm, "end": v(-228.6, 145.34) * mm});
            skLineSegment(sketch, "E784", {"start": v(-228.6, 145.34) * mm, "end": v(-228.6, 161.38) * mm});
            skLineSegment(sketch, "E785", {"start": v(-223.84, 161.38) * mm, "end": v(-228.6, 161.38) * mm});
            skLineSegment(sketch, "E786", {"start": v(-223.84, 161.38) * mm, "end": v(-223.84, 177.43) * mm});
            skLineSegment(sketch, "E787", {"start": v(-223.84, 177.43) * mm, "end": v(-228.6, 177.43) * mm});
            skLineSegment(sketch, "E788", {"start": v(-228.6, 177.43) * mm, "end": v(-228.6, 193.47) * mm});
            skLineSegment(sketch, "E789", {"start": v(-223.84, 193.47) * mm, "end": v(-228.6, 193.47) * mm});
            skLineSegment(sketch, "E790", {"start": v(-223.84, 193.47) * mm, "end": v(-223.84, 209.5) * mm});
            skLineSegment(sketch, "E791", {"start": v(-223.84, 209.5) * mm, "end": v(-228.6, 209.5) * mm});
            skLineSegment(sketch, "E792", {"start": v(-228.6, 209.5) * mm, "end": v(-228.6, 225.55) * mm});
            skLineSegment(sketch, "E793", {"start": v(-223.84, 225.55) * mm, "end": v(-228.6, 225.55) * mm});
            skLineSegment(sketch, "E794", {"start": v(-223.84, 225.55) * mm, "end": v(-223.84, 241.6) * mm});
            skLineSegment(sketch, "E795", {"start": v(-223.84, 241.6) * mm, "end": v(-228.6, 241.6) * mm});
            skLineSegment(sketch, "E796", {"start": v(-228.6, 241.6) * mm, "end": v(-228.6, 257.64) * mm});
            skLineSegment(sketch, "E797", {"start": v(-223.84, 257.64) * mm, "end": v(-228.6, 257.64) * mm});
            skLineSegment(sketch, "E798", {"start": v(-223.84, 257.64) * mm, "end": v(-223.84, 273.68) * mm});
            skLineSegment(sketch, "E799", {"start": v(-223.84, 273.68) * mm, "end": v(-228.6, 273.68) * mm});
            skLineSegment(sketch, "E800", {"start": v(-228.6, 273.68) * mm, "end": v(-228.6, 289.72) * mm});
            skLineSegment(sketch, "E801", {"start": v(-223.84, 289.72) * mm, "end": v(-228.6, 289.72) * mm});
            skLineSegment(sketch, "E802", {"start": v(-223.84, 289.72) * mm, "end": v(-223.84, 305.76) * mm});
            skLineSegment(sketch, "E803", {"start": v(-223.84, 305.76) * mm, "end": v(-228.6, 305.76) * mm});
            skLineSegment(sketch, "E804", {"start": v(-228.6, 305.76) * mm, "end": v(-228.6, 321.8) * mm});
            skLineSegment(sketch, "E805", {"start": v(-223.84, 321.8) * mm, "end": v(-228.6, 321.8) * mm});
            skLineSegment(sketch, "E806", {"start": v(-223.84, 321.8) * mm, "end": v(-223.84, 337.85) * mm});
            skLineSegment(sketch, "E807", {"start": v(-223.84, 337.85) * mm, "end": v(-228.6, 337.85) * mm});
            skLineSegment(sketch, "E808", {"start": v(-228.6, 337.85) * mm, "end": v(-228.6, 353.89) * mm});
            skLineSegment(sketch, "E809", {"start": v(-223.84, 353.89) * mm, "end": v(-228.6, 353.89) * mm});
            skLineSegment(sketch, "E810", {"start": v(-223.84, 353.89) * mm, "end": v(-223.84, 369.93) * mm});
            skLineSegment(sketch, "E811", {"start": v(-223.84, 369.93) * mm, "end": v(-228.6, 369.93) * mm});
            skLineSegment(sketch, "E812", {"start": v(-228.6, 369.93) * mm, "end": v(-228.6, 385.97) * mm});
            skLineSegment(sketch, "E813", {"start": v(-223.84, 385.97) * mm, "end": v(-228.6, 385.97) * mm});
            skLineSegment(sketch, "E814", {"start": v(-223.84, 385.97) * mm, "end": v(-223.84, 402.02) * mm});
            skLineSegment(sketch, "E815", {"start": v(-223.84, 402.02) * mm, "end": v(-228.6, 402.02) * mm});
            skLineSegment(sketch, "E816", {"start": v(-228.6, 402.02) * mm, "end": v(-228.6, 418.06) * mm});
            skLineSegment(sketch, "E817", {"start": v(-223.84, 418.06) * mm, "end": v(-228.6, 418.06) * mm});
            skLineSegment(sketch, "E818", {"start": v(-223.84, 418.06) * mm, "end": v(-223.84, 429.34) * mm});
            skLineSegment(sketch, "E819", {"start": v(223.84, 134.06) * mm, "end": v(223.84, 145.34) * mm});
            skLineSegment(sketch, "E820", {"start": v(228.6, 145.34) * mm, "end": v(223.84, 145.34) * mm});
            skLineSegment(sketch, "E821", {"start": v(228.6, 145.34) * mm, "end": v(228.6, 161.38) * mm});
            skLineSegment(sketch, "E822", {"start": v(228.6, 161.38) * mm, "end": v(223.84, 161.38) * mm});
            skLineSegment(sketch, "E823", {"start": v(223.84, 161.38) * mm, "end": v(223.84, 177.43) * mm});
            skLineSegment(sketch, "E824", {"start": v(228.6, 177.43) * mm, "end": v(223.84, 177.43) * mm});
            skLineSegment(sketch, "E825", {"start": v(228.6, 177.43) * mm, "end": v(228.6, 193.47) * mm});
            skLineSegment(sketch, "E826", {"start": v(228.6, 193.47) * mm, "end": v(223.84, 193.47) * mm});
            skLineSegment(sketch, "E827", {"start": v(223.84, 193.47) * mm, "end": v(223.84, 209.5) * mm});
            skLineSegment(sketch, "E828", {"start": v(228.6, 209.5) * mm, "end": v(223.84, 209.5) * mm});
            skLineSegment(sketch, "E829", {"start": v(228.6, 209.5) * mm, "end": v(228.6, 225.55) * mm});
            skLineSegment(sketch, "E830", {"start": v(228.6, 225.55) * mm, "end": v(223.84, 225.55) * mm});
            skLineSegment(sketch, "E831", {"start": v(223.84, 225.55) * mm, "end": v(223.84, 241.6) * mm});
            skLineSegment(sketch, "E832", {"start": v(228.6, 241.6) * mm, "end": v(223.84, 241.6) * mm});
            skLineSegment(sketch, "E833", {"start": v(228.6, 241.6) * mm, "end": v(228.6, 257.64) * mm});
            skLineSegment(sketch, "E834", {"start": v(228.6, 257.64) * mm, "end": v(223.84, 257.64) * mm});
            skLineSegment(sketch, "E835", {"start": v(223.84, 257.64) * mm, "end": v(223.84, 273.68) * mm});
            skLineSegment(sketch, "E836", {"start": v(228.6, 273.68) * mm, "end": v(223.84, 273.68) * mm});
            skLineSegment(sketch, "E837", {"start": v(228.6, 273.68) * mm, "end": v(228.6, 289.72) * mm});
            skLineSegment(sketch, "E838", {"start": v(228.6, 289.72) * mm, "end": v(223.84, 289.72) * mm});
            skLineSegment(sketch, "E839", {"start": v(223.84, 289.72) * mm, "end": v(223.84, 305.76) * mm});
            skLineSegment(sketch, "E840", {"start": v(228.6, 305.76) * mm, "end": v(223.84, 305.76) * mm});
            skLineSegment(sketch, "E841", {"start": v(228.6, 305.76) * mm, "end": v(228.6, 321.8) * mm});
            skLineSegment(sketch, "E842", {"start": v(228.6, 321.8) * mm, "end": v(223.84, 321.8) * mm});
            skLineSegment(sketch, "E843", {"start": v(223.84, 321.8) * mm, "end": v(223.84, 337.85) * mm});
            skLineSegment(sketch, "E844", {"start": v(228.6, 337.85) * mm, "end": v(223.84, 337.85) * mm});
            skLineSegment(sketch, "E845", {"start": v(228.6, 337.85) * mm, "end": v(228.6, 353.89) * mm});
            skLineSegment(sketch, "E846", {"start": v(228.6, 353.89) * mm, "end": v(223.84, 353.89) * mm});
            skLineSegment(sketch, "E847", {"start": v(223.84, 353.89) * mm, "end": v(223.84, 369.93) * mm});
            skLineSegment(sketch, "E848", {"start": v(228.6, 369.93) * mm, "end": v(223.84, 369.93) * mm});
            skLineSegment(sketch, "E849", {"start": v(228.6, 369.93) * mm, "end": v(228.6, 385.97) * mm});
            skLineSegment(sketch, "E850", {"start": v(228.6, 385.97) * mm, "end": v(223.84, 385.97) * mm});
            skLineSegment(sketch, "E851", {"start": v(223.84, 385.97) * mm, "end": v(223.84, 402.02) * mm});
            skLineSegment(sketch, "E852", {"start": v(228.6, 402.02) * mm, "end": v(223.84, 402.02) * mm});
            skLineSegment(sketch, "E853", {"start": v(228.6, 402.02) * mm, "end": v(228.6, 418.06) * mm});
            skLineSegment(sketch, "E854", {"start": v(228.6, 418.06) * mm, "end": v(223.84, 418.06) * mm});
            skLineSegment(sketch, "E855", {"start": v(223.84, 418.06) * mm, "end": v(223.84, 429.34) * mm});
            skLineSegment(sketch, "E856", {"start": v(0, 119.3) * mm, "end": v(0, 5) * mm, "construction": true});
            skLineSegment(sketch, "E857", {"start": v(-223.84, 62.15) * mm, "end": v(228.6, 62.15) * mm, "construction": true});
            skLineSegment(sketch, "E858", {"start": v(0, -319.8) * mm, "end": v(0, -434.1) * mm, "construction": true});
            skLineSegment(sketch, "E859", {"start": v(228.6, -376.95) * mm, "end": v(-223.84, -376.95) * mm, "construction": true});
            skCircle(sketch, "E860", {"center": v(-165.1, 62.15) * mm, "radius": 30.16 * mm});
            skCircle(sketch, "E861", {"center": v(165.11, 62.15) * mm, "radius": 30.16 * mm});
            skCircle(sketch, "E862", {"center": v(-174.62, -376.95) * mm, "radius": 30.16 * mm});
            skCircle(sketch, "E863", {"center": v(174.63, -376.95) * mm, "radius": 30.16 * mm});
            skSolve(sketch);
        }
        {
            var Q0;
            Q0=makeQuery(id+"F0.imprint","IMPRINT",FACE,{"disambiguationData":[TD([[makeQuery(id+"F0.imprint","IMPRINT",EDGE,{"derivedFrom":sQuery(id+"F0.wireOp",EDGE,"E668")}),1.0]])]});
            var Q1;
            Q1=makeQuery(id+"F0.imprint","IMPRINT",FACE,{"disambiguationData":[TD([[makeQuery(id+"F0.imprint","IMPRINT",EDGE,{"derivedFrom":sQuery(id+"F0.wireOp",EDGE,"E528")}),1.0]])]});
            var Q2;
            Q2=makeQuery(id+"F0.imprint","IMPRINT",FACE,{"disambiguationData":[TD([[makeQuery(id+"F0.imprint","IMPRINT",EDGE,{"derivedFrom":sQuery(id+"F0.wireOp",EDGE,"E240")}),1.0]])]});
            var Q3;
            Q3=makeQuery(id+"F0.imprint","IMPRINT",FACE,{"disambiguationData":[TD([[makeQuery(id+"F0.imprint","IMPRINT",EDGE,{"derivedFrom":sQuery(id+"F0.wireOp",EDGE,"E140")}),1.0]])]});
            var Q4;
            Q4=makeQuery(id+"F0.imprint","IMPRINT",FACE,{"disambiguationData":[TD([[makeQuery(id+"F0.imprint","IMPRINT",EDGE,{"derivedFrom":sQuery(id+"F0.wireOp",EDGE,"E0")}),1.0]])]});
            var Q5;
            Q5=makeQuery(id+"F0.imprint","IMPRINT",FACE,{"disambiguationData":[TD([[makeQuery(id+"F0.imprint","IMPRINT",EDGE,{"derivedFrom":sQuery(id+"F0.wireOp",EDGE,"E428")}),1.0]])]});
            extrude(context, id + "F1", {"entities" : qUnion([Q0, Q1, Q2, Q3, Q4, Q5]), "depth" : 25.4 * mm});
        }
    });
